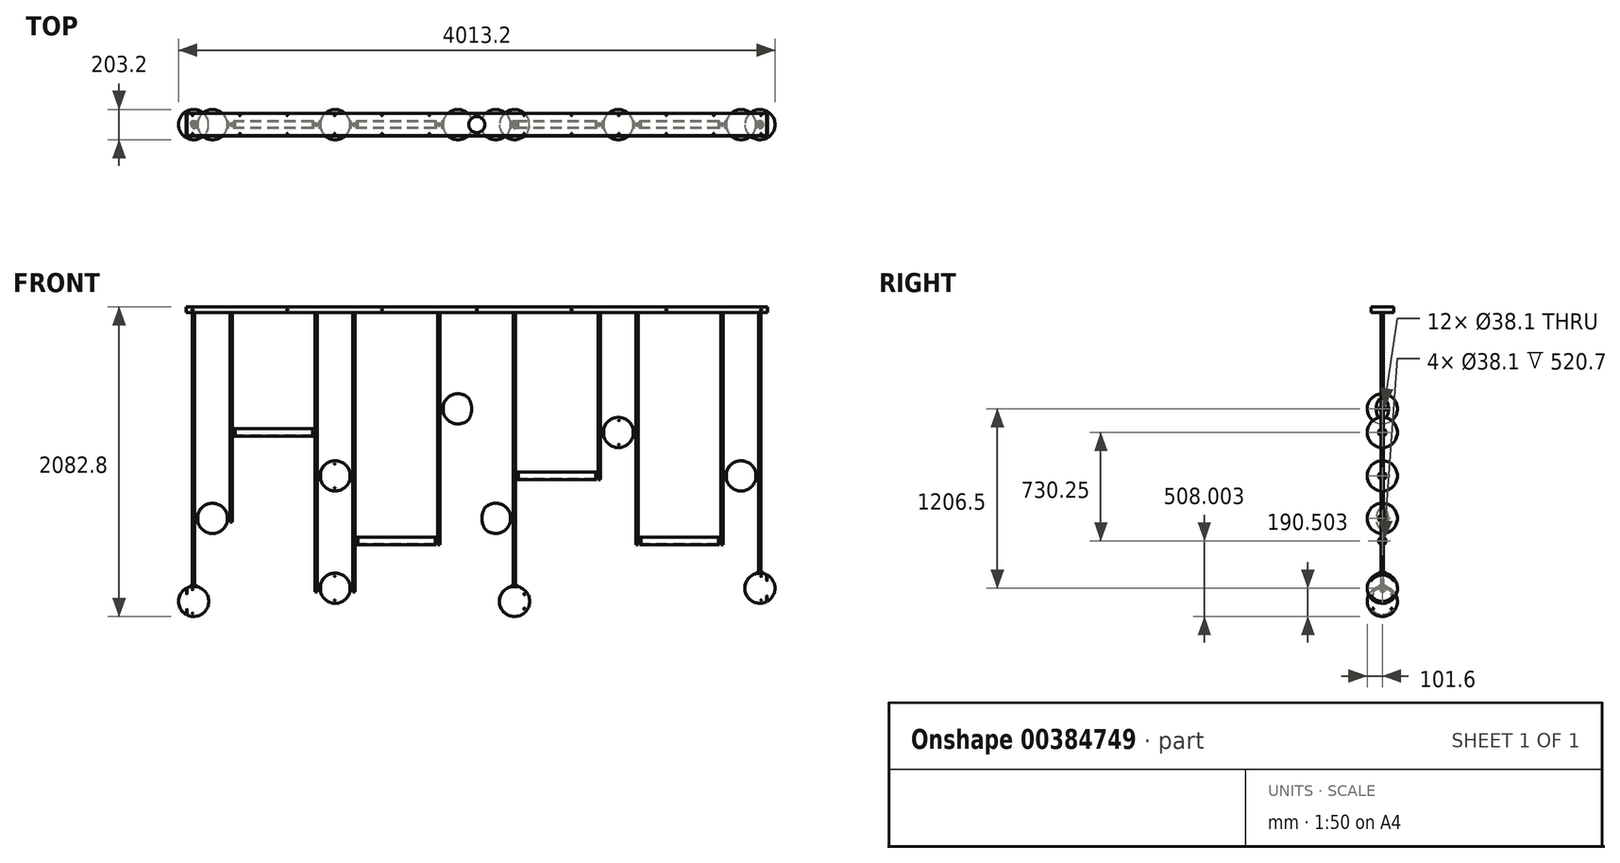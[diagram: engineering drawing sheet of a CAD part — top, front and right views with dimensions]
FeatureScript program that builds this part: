
annotation { "Feature Type Name" : "Feature", "Feature Type Description" : "" }
export const myFeature = defineFeature(function(context is Context, id is Id, definition is map)
    precondition{}
    {
        {
            var Q0;
            Q0=qCreatedBy(makeId("Front.planeOp"),FACE);
            var sketch = newSketch(context, id + "F0", { "sketchPlane" : qUnion([Q0])});
            skLineSegment(sketch, "E0.bottom", {"start": v(-1955.8, 1091.47) * mm, "end": v(1955.8, 1091.47) * mm});
            skLineSegment(sketch, "E0.top", {"start": v(-1955.8, 1053.37) * mm, "end": v(1955.8, 1053.37) * mm});
            skLineSegment(sketch, "E0.left", {"start": v(-1955.8, 1091.47) * mm, "end": v(-1955.8, 1053.37) * mm});
            skLineSegment(sketch, "E0.right", {"start": v(1955.8, 1091.47) * mm, "end": v(1955.8, 1053.37) * mm});
            skLineSegment(sketch, "E1", {"start": v(0, 0) * mm, "end": v(0, 1053.37) * mm, "construction": true});
            skLineSegment(sketch, "E2", {"start": v(-1905, 1053.37) * mm, "end": v(-1905, -788.13) * mm, "construction": true});
            skCircle(sketch, "E3", {"center": v(-1905, -889.73) * mm, "radius": 101.6 * mm});
            skLineSegment(sketch, "E4", {"start": v(-1651, 1053.37) * mm, "end": v(-1651, -788.13) * mm, "construction": true});
            skLineSegment(sketch, "E5", {"start": v(-1079.5, 1053.37) * mm, "end": v(-1079.5, -788.13) * mm, "construction": true});
            skLineSegment(sketch, "E6", {"start": v(-825.5, 1053.37) * mm, "end": v(-825.5, -788.13) * mm, "construction": true});
            skLineSegment(sketch, "E7", {"start": v(-254, 1053.37) * mm, "end": v(-254, -788.13) * mm, "construction": true});
            skLineSegment(sketch, "E8", {"start": v(0, 1053.37) * mm, "end": v(0, -788.13) * mm, "construction": true});
            skLineSegment(sketch, "E9", {"start": v(254, 1053.37) * mm, "end": v(254, -788.13) * mm, "construction": true});
            skLineSegment(sketch, "E10", {"start": v(-1905, -788.13) * mm, "end": v(1787.4, -788.13) * mm, "construction": true});
            skLineSegment(sketch, "E11", {"start": v(825.5, 1053.37) * mm, "end": v(825.5, -788.13) * mm, "construction": true});
            skLineSegment(sketch, "E12", {"start": v(1079.5, 1053.37) * mm, "end": v(1079.5, -788.13) * mm, "construction": true});
            skLineSegment(sketch, "E13", {"start": v(1651, 1053.37) * mm, "end": v(1651, -788.13) * mm, "construction": true});
            skLineSegment(sketch, "E14", {"start": v(1905, 1053.37) * mm, "end": v(1905, -788.13) * mm, "construction": true});
            skLineSegment(sketch, "E15", {"start": v(-1955.8, 1091.47) * mm, "end": v(-1955.8, -788.13) * mm, "construction": true});
            skLineSegment(sketch, "E16", {"start": v(1955.8, 1053.37) * mm, "end": v(1955.8, -788.13) * mm, "construction": true});
            skLineSegment(sketch, "E17", {"start": v(1955.8, -91.24) * mm, "end": v(1905, -91.24) * mm, "construction": true});
            skLineSegment(sketch, "E18", {"start": v(-1955.8, -396.8) * mm, "end": v(-1905, -396.8) * mm, "construction": true});
            skLineSegment(sketch, "E19", {"start": v(-1651, 246.92) * mm, "end": v(-1079.5, 246.92) * mm, "construction": true});
            skLineSegment(sketch, "E20", {"start": v(1079.5, -483.33) * mm, "end": v(1651, -483.33) * mm, "construction": true});
            skLineSegment(sketch, "E21", {"start": v(-1079.5, -45.18) * mm, "end": v(-825.5, -45.18) * mm, "construction": true});
            skLineSegment(sketch, "E22", {"start": v(-254, 405.67) * mm, "end": v(0, 405.67) * mm, "construction": true});
            skLineSegment(sketch, "E23", {"start": v(0, -330.93) * mm, "end": v(254, -330.93) * mm, "construction": true});
            skLineSegment(sketch, "E24", {"start": v(1651, -45.18) * mm, "end": v(1905, -45.18) * mm, "construction": true});
            skLineSegment(sketch, "E25", {"start": v(-1905, -330.93) * mm, "end": v(-1651, -330.93) * mm, "construction": true});
            skCircle(sketch, "E26", {"center": v(-1778, -330.93) * mm, "radius": 101.6 * mm});
            skCircle(sketch, "E27", {"center": v(-952.5, -45.18) * mm, "radius": 101.6 * mm});
            skCircle(sketch, "E28", {"center": v(-127, 405.67) * mm, "radius": 101.6 * mm});
            skCircle(sketch, "E29", {"center": v(127, -330.93) * mm, "radius": 101.6 * mm});
            skCircle(sketch, "E30", {"center": v(1778, -45.18) * mm, "radius": 101.6 * mm});
            skLineSegment(sketch, "E31", {"start": v(-1079.5, -800.83) * mm, "end": v(-825.5, -800.83) * mm, "construction": true});
            skCircle(sketch, "E32", {"center": v(-952.5, -800.83) * mm, "radius": 101.6 * mm});
            skCircle(sketch, "E33", {"center": v(254, -889.73) * mm, "radius": 101.6 * mm});
            skCircle(sketch, "E34", {"center": v(1905, -800.83) * mm, "radius": 101.6 * mm});
            skLineSegment(sketch, "E35", {"start": v(254, -991.33) * mm, "end": v(-1905, -991.33) * mm, "construction": true});
            skLineSegment(sketch, "E36.bottom", {"start": v(-1625.6, 272.32) * mm, "end": v(-1104.9, 272.32) * mm});
            skLineSegment(sketch, "E36.top", {"start": v(-1625.6, 221.52) * mm, "end": v(-1104.9, 221.52) * mm});
            skLineSegment(sketch, "E36.left", {"start": v(-1625.6, 272.32) * mm, "end": v(-1625.6, 221.52) * mm});
            skLineSegment(sketch, "E36.right", {"start": v(-1104.9, 272.32) * mm, "end": v(-1104.9, 221.52) * mm});
            skPoint(sketch, "E36.middle", {"position": v(-1365.25, 246.92) * mm});
            skLineSegment(sketch, "E37.bottom", {"start": v(1104.9, -457.93) * mm, "end": v(1625.6, -457.93) * mm});
            skLineSegment(sketch, "E37.top", {"start": v(1104.9, -508.73) * mm, "end": v(1625.6, -508.73) * mm});
            skLineSegment(sketch, "E37.left", {"start": v(1104.9, -457.93) * mm, "end": v(1104.9, -508.73) * mm});
            skLineSegment(sketch, "E37.right", {"start": v(1625.6, -457.93) * mm, "end": v(1625.6, -508.73) * mm});
            skPoint(sketch, "E37.middle", {"position": v(1365.25, -483.33) * mm});
            skLineSegment(sketch, "E38", {"start": v(254, -45.18) * mm, "end": v(825.5, -45.18) * mm, "construction": true});
            skLineSegment(sketch, "E39.bottom", {"start": v(800.1, -70.58) * mm, "end": v(279.4, -70.58) * mm});
            skLineSegment(sketch, "E39.top", {"start": v(800.1, -19.78) * mm, "end": v(279.4, -19.78) * mm});
            skLineSegment(sketch, "E39.left", {"start": v(800.1, -19.78) * mm, "end": v(800.1, -70.58) * mm});
            skLineSegment(sketch, "E39.right", {"start": v(279.4, -19.78) * mm, "end": v(279.4, -70.58) * mm});
            skPoint(sketch, "E39.middle", {"position": v(539.75, -45.18) * mm});
            skLineSegment(sketch, "E40", {"start": v(825.5, 246.92) * mm, "end": v(1079.5, 246.92) * mm, "construction": true});
            skCircle(sketch, "E41", {"center": v(952.5, 246.92) * mm, "radius": 101.6 * mm});
            skLineSegment(sketch, "E42", {"start": v(-825.5, -483.33) * mm, "end": v(-254, -483.33) * mm, "construction": true});
            skLineSegment(sketch, "E43.bottom", {"start": v(-800.1, -457.93) * mm, "end": v(-279.4, -457.93) * mm});
            skLineSegment(sketch, "E43.top", {"start": v(-800.1, -508.73) * mm, "end": v(-279.4, -508.73) * mm});
            skLineSegment(sketch, "E43.left", {"start": v(-800.1, -457.93) * mm, "end": v(-800.1, -508.73) * mm});
            skLineSegment(sketch, "E43.right", {"start": v(-279.4, -457.93) * mm, "end": v(-279.4, -508.73) * mm});
            skPoint(sketch, "E43.middle", {"position": v(-539.75, -483.33) * mm});
            skLineSegment(sketch, "E44", {"start": v(127, -330.93) * mm, "end": v(127, 405.67) * mm, "construction": true});
            skLineSegment(sketch, "E45", {"start": v(-952.5, -45.18) * mm, "end": v(-952.5, -800.83) * mm, "construction": true});
            skLineSegment(sketch, "E46", {"start": v(-127, 405.67) * mm, "end": v(-127, -800.83) * mm, "construction": true});
            skLineSegment(sketch, "E47", {"start": v(952.5, 246.92) * mm, "end": v(952.5, -330.93) * mm, "construction": true});
            skLineSegment(sketch, "E48", {"start": v(1778, -45.18) * mm, "end": v(1778, 246.92) * mm, "construction": true});
            skLineSegment(sketch, "E49", {"start": v(-1206.5, -45.18) * mm, "end": v(-1206.5, -330.93) * mm, "construction": true});
            skLineSegment(sketch, "E50", {"start": v(-1778, 0) * mm, "end": v(-952.5, 0) * mm, "construction": true});
            skLineSegment(sketch, "E51", {"start": v(-952.5, -423) * mm, "end": v(-127, -423) * mm, "construction": true});
            skLineSegment(sketch, "E52", {"start": v(127, 0) * mm, "end": v(952.5, 0) * mm, "construction": true});
            skLineSegment(sketch, "E53", {"start": v(952.5, 686.49) * mm, "end": v(1778, 686.49) * mm, "construction": true});
            skLineSegment(sketch, "E54", {"start": v(254, -991.33) * mm, "end": v(1905, -991.33) * mm, "construction": true});
            skLineSegment(sketch, "E55", {"start": v(1905, -800.83) * mm, "end": v(1905, -889.73) * mm, "construction": true});
            skSolve(sketch);
        }
        {
            var Q0;
            Q0=qCreatedBy(makeId("Front.planeOp"),FACE);
            var sketch = newSketch(context, id + "F1", { "sketchPlane" : qUnion([Q0])});
            skLineSegment(sketch, "E56.0.0", {"start": v(-1955.8, 1091.47) * mm, "end": v(-1955.8, 1053.37) * mm});
            skLineSegment(sketch, "E56.0.1", {"start": v(-1955.8, 1053.37) * mm, "end": v(1955.8, 1053.37) * mm});
            skLineSegment(sketch, "E56.0.2", {"start": v(1955.8, 1053.37) * mm, "end": v(1955.8, 1091.47) * mm});
            skLineSegment(sketch, "E56.0.3", {"start": v(1955.8, 1091.47) * mm, "end": v(-1955.8, 1091.47) * mm});
            skSolve(sketch);
        }
        {
            var Q0;
            Q0 = qSketchRegion(id + "F1", true);
            extrude(context, id + "F2", {"entities" : qUnion([Q0]), "depth" : 76.2 * mm, "hasSecondDirection" : true, "secondDirectionOppositeDirection" : true, "secondDirectionDepth" : 76.2 * mm});
        }
        {
            var Q0;
            Q0=qCreatedBy(makeId("Front.planeOp"),FACE);
            var sketch = newSketch(context, id + "F3", { "sketchPlane" : qUnion([Q0])});
            skArc(sketch, "E57.6", {"start": v(-1678.2, -311.88) * mm, "mid": v(-1778, -229.33) * mm, "end": v(-1877.8, -311.88) * mm});
            skArc(sketch, "E58.0", {"start": v(-1679.82, -311.88) * mm, "mid": v(-1778, -230.91) * mm, "end": v(-1876.18, -311.88) * mm});
            skLineSegment(sketch, "E59.0", {"start": v(-1905, -349.98) * mm, "end": v(-1651, -349.98) * mm, "construction": true});
            skLineSegment(sketch, "E60.0", {"start": v(-1905, -330.93) * mm, "end": v(-1651, -330.93) * mm, "construction": true});
            skLineSegment(sketch, "E61.MirrorCS", {"start": v(-1905, -311.88) * mm, "end": v(-1651, -311.88) * mm, "construction": true});
            skLineSegment(sketch, "E62", {"start": v(-1679.82, -311.88) * mm, "end": v(-1678.2, -311.88) * mm});
            skLineSegment(sketch, "E63", {"start": v(-1877.8, -311.88) * mm, "end": v(-1876.18, -311.88) * mm});
            skSolve(sketch);
        }
        {
            var Q0;
            Q0 = qSketchRegion(id + "F3", true);
            var Q1;
            Q1=sQuery(id+"F3.wireOp",EDGE,"E60.0");
            revolve(context, id + "F4", {"entities" : qUnion([Q0]), "axis" : qUnion([Q1]), "revolveType" : RevolveType.FULL});
        }
        {
            var Q0;
            Q0=qCreatedBy(makeId("Front.planeOp"),FACE);
            var sketch = newSketch(context, id + "F5", { "sketchPlane" : qUnion([Q0])});
            skLineSegment(sketch, "E64.0", {"start": v(-1678.2, -349.98) * mm, "end": v(-1678.2, -311.88) * mm, "construction": true});
            skCircle(sketch, "E65.1", {"center": v(-1778, -330.93) * mm, "radius": 101.6 * mm, "construction": true});
            skLineSegment(sketch, "E66.bottom", {"start": v(-1671.69, -330.93) * mm, "end": v(-1679.63, -330.93) * mm});
            skLineSegment(sketch, "E66.top", {"start": v(-1671.69, -305.53) * mm, "end": v(-1679.63, -305.53) * mm});
            skLineSegment(sketch, "E66.left", {"start": v(-1671.69, -330.93) * mm, "end": v(-1671.69, -305.53) * mm});
            skLineSegment(sketch, "E66.right", {"start": v(-1679.63, -330.93) * mm, "end": v(-1679.63, -305.53) * mm});
            skLineSegment(sketch, "E67.bottom", {"start": v(-1671.69, -330.93) * mm, "end": v(-1651, -330.93) * mm});
            skLineSegment(sketch, "E67.top", {"start": v(-1671.69, -324.58) * mm, "end": v(-1651, -324.58) * mm});
            skLineSegment(sketch, "E67.left", {"start": v(-1671.69, -330.93) * mm, "end": v(-1671.69, -324.58) * mm});
            skLineSegment(sketch, "E67.right", {"start": v(-1651, -330.93) * mm, "end": v(-1651, -324.58) * mm});
            skLineSegment(sketch, "E68.0", {"start": v(-1651, 1053.37) * mm, "end": v(-1651, -788.13) * mm, "construction": true});
            skLineSegment(sketch, "E69", {"start": v(-1778, -330.93) * mm, "end": v(-1778, -333.62) * mm, "construction": true});
            skLineSegment(sketch, "E70.MirrorCS", {"start": v(-1884.31, -305.53) * mm, "end": v(-1876.37, -305.53) * mm});
            skLineSegment(sketch, "E71.MirrorCS", {"start": v(-1884.31, -330.93) * mm, "end": v(-1876.37, -330.93) * mm});
            skLineSegment(sketch, "E72.MirrorCS", {"start": v(-1905, -330.93) * mm, "end": v(-1905, -324.58) * mm});
            skLineSegment(sketch, "E73.MirrorCS", {"start": v(-1884.31, -330.93) * mm, "end": v(-1884.31, -324.58) * mm});
            skLineSegment(sketch, "E74.MirrorCS", {"start": v(-1884.31, -324.58) * mm, "end": v(-1905, -324.58) * mm});
            skLineSegment(sketch, "E75.MirrorCS", {"start": v(-1884.31, -330.93) * mm, "end": v(-1905, -330.93) * mm});
            skLineSegment(sketch, "E76.MirrorCS", {"start": v(-1876.37, -330.93) * mm, "end": v(-1876.37, -305.53) * mm});
            skLineSegment(sketch, "E77.MirrorCS", {"start": v(-1884.31, -330.93) * mm, "end": v(-1884.31, -305.53) * mm});
            skSolve(sketch);
        }
        {
            var Q0;
            Q0 = qSketchRegion(id + "F5", true);
            var Q1;
            Q1=sQuery(id+"F5.wireOp",EDGE,"E67.bottom");
            revolve(context, id + "F6", {"entities" : qUnion([Q0]), "axis" : qUnion([Q1]), "revolveType" : RevolveType.FULL});
        }
        {
            var Q0;
            Q0=qCreatedBy(makeId("Front.planeOp"),FACE);
            var sketch = newSketch(context, id + "F7", { "sketchPlane" : qUnion([Q0])});
            skLineSegment(sketch, "E78.0", {"start": v(-1905, 1053.37) * mm, "end": v(-1905, -788.13) * mm, "construction": true});
            skLineSegment(sketch, "E79.0", {"start": v(-1905, -330.93) * mm, "end": v(-1651, -330.93) * mm, "construction": true});
            skLineSegment(sketch, "E80", {"start": v(-1778, -330.93) * mm, "end": v(-1778, -44.72) * mm, "construction": true});
            skLineSegment(sketch, "E81.bottom", {"start": v(-1905, -305.53) * mm, "end": v(-1912.94, -305.53) * mm});
            skLineSegment(sketch, "E81.top", {"start": v(-1905, -356.33) * mm, "end": v(-1912.94, -356.33) * mm});
            skLineSegment(sketch, "E81.left", {"start": v(-1905, -305.53) * mm, "end": v(-1905, -356.33) * mm});
            skLineSegment(sketch, "E81.right", {"start": v(-1912.94, -305.53) * mm, "end": v(-1912.94, -356.33) * mm});
            skPoint(sketch, "E82", {"position": v(-1905, -330.93) * mm});
            skLineSegment(sketch, "E83.MirrorCS", {"start": v(-1643.06, -305.53) * mm, "end": v(-1643.06, -356.33) * mm});
            skLineSegment(sketch, "E84.MirrorCS", {"start": v(-1651, -305.53) * mm, "end": v(-1651, -356.33) * mm});
            skLineSegment(sketch, "E85.MirrorCS", {"start": v(-1651, -356.33) * mm, "end": v(-1643.06, -356.33) * mm});
            skLineSegment(sketch, "E86.MirrorCS", {"start": v(-1651, -305.53) * mm, "end": v(-1643.06, -305.53) * mm});
            skPoint(sketch, "E87.MirrorP", {"position": v(-1651, -330.93) * mm});
            skSolve(sketch);
        }
        {
            var Q0;
            Q0=makeQuery(id+"F7.imprint","IMPRINT",FACE,{"disambiguationData":[TD([[makeQuery(id+"F7.imprint","IMPRINT",EDGE,{"derivedFrom":sQuery(id+"F7.wireOp",EDGE,"E81.bottom")}),1.0]])]});
            var Q1;
            Q1=sQuery(id+"F7.wireOp",EDGE,"E78.0");
            revolve(context, id + "F8", {"entities" : qUnion([Q0]), "axis" : qUnion([Q1]), "revolveType" : RevolveType.FULL});
        }
        {
            var Q0;
            Q0=makeQuery(id+"F7.imprint","IMPRINT",FACE,{"disambiguationData":[TD([[makeQuery(id+"F7.imprint","IMPRINT",EDGE,{"derivedFrom":sQuery(id+"F7.wireOp",EDGE,"E83.MirrorCS")}),-1.0]])]});
            var Q1;
            Q1=sQuery(id+"F0.wireOp",EDGE,"E4");
            revolve(context, id + "F9", {"entities" : qUnion([Q0]), "axis" : qUnion([Q1]), "revolveType" : RevolveType.FULL});
        }
        {
            var Q0;
            Q0=makeQuery(id+"F6.opRevolve","SWEPT_BODY",BODY,{"disambiguationData":[OSD([sQuery(id+"F5.wireOp",EDGE,"E70.MirrorCS"),sQuery(id+"F5.wireOp",EDGE,"E71.MirrorCS"),sQuery(id+"F5.wireOp",EDGE,"E72.MirrorCS"),sQuery(id+"F5.wireOp",EDGE,"E74.MirrorCS"),sQuery(id+"F5.wireOp",EDGE,"E75.MirrorCS"),sQuery(id+"F5.wireOp",EDGE,"E76.MirrorCS"),sQuery(id+"F5.wireOp",EDGE,"E77.MirrorCS")])]});
            var Q1;
            Q1=makeQuery(id+"F6.opRevolve","SWEPT_BODY",BODY,{"disambiguationData":[OSD([sQuery(id+"F5.wireOp",EDGE,"E66.bottom"),sQuery(id+"F5.wireOp",EDGE,"E66.top"),sQuery(id+"F5.wireOp",EDGE,"E66.left"),sQuery(id+"F5.wireOp",EDGE,"E66.right"),sQuery(id+"F5.wireOp",EDGE,"E67.bottom"),sQuery(id+"F5.wireOp",EDGE,"E67.top"),sQuery(id+"F5.wireOp",EDGE,"E67.right")])]});
            var Q2;
            Q2=makeQuery(id+"F4.opRevolve","SWEPT_BODY",BODY,{"disambiguationData":[OSD([sQuery(id+"F3.wireOp",EDGE,"E57.6"),sQuery(id+"F3.wireOp",EDGE,"E58.0"),sQuery(id+"F3.wireOp",EDGE,"E62"),sQuery(id+"F3.wireOp",EDGE,"E63")])]});
            var Q3;
            Q3=makeQuery(id+"F8.opRevolve","SWEPT_BODY",BODY,{"disambiguationData":[OSD([sQuery(id+"F7.wireOp",EDGE,"E81.bottom"),sQuery(id+"F7.wireOp",EDGE,"E81.top"),sQuery(id+"F7.wireOp",EDGE,"E81.left"),sQuery(id+"F7.wireOp",EDGE,"E81.right")])]});
            var Q4;
            Q4=makeQuery(id+"F9.opRevolve","SWEPT_BODY",BODY,{"disambiguationData":[OSD([sQuery(id+"F7.wireOp",EDGE,"E83.MirrorCS"),sQuery(id+"F7.wireOp",EDGE,"E84.MirrorCS"),sQuery(id+"F7.wireOp",EDGE,"E85.MirrorCS"),sQuery(id+"F7.wireOp",EDGE,"E86.MirrorCS")])]});
            var Q5;
            Q5=sQuery(id+"F0.wireOp",EDGE,"E50");
            transform(context, id + "F10", {"entities" : qUnion([Q0, Q1, Q2, Q3, Q4]), "transformType" : TransformType.TRANSLATION_ENTITY, "oppositeDirectionEntity" : false, "transformLine" : qUnion([Q5]), "makeCopy" : true});
        }
        {
            var Q0;
            Q0=makeQuery(id+"F10.opPattern","COPY",BODY,{"derivedFrom":makeQuery(id+"F6.opRevolve","SWEPT_BODY",BODY,{"disambiguationData":[OSD([sQuery(id+"F5.wireOp",EDGE,"E66.bottom"),sQuery(id+"F5.wireOp",EDGE,"E66.top"),sQuery(id+"F5.wireOp",EDGE,"E66.left"),sQuery(id+"F5.wireOp",EDGE,"E66.right"),sQuery(id+"F5.wireOp",EDGE,"E67.bottom"),sQuery(id+"F5.wireOp",EDGE,"E67.top"),sQuery(id+"F5.wireOp",EDGE,"E67.right")])]}),"instanceName":"1"});
            var Q1;
            Q1=makeQuery(id+"F10.opPattern","COPY",BODY,{"derivedFrom":makeQuery(id+"F4.opRevolve","SWEPT_BODY",BODY,{"disambiguationData":[OSD([sQuery(id+"F3.wireOp",EDGE,"E57.6"),sQuery(id+"F3.wireOp",EDGE,"E58.0"),sQuery(id+"F3.wireOp",EDGE,"E62"),sQuery(id+"F3.wireOp",EDGE,"E63")])]}),"instanceName":"1"});
            var Q2;
            Q2=makeQuery(id+"F10.opPattern","COPY",BODY,{"derivedFrom":makeQuery(id+"F6.opRevolve","SWEPT_BODY",BODY,{"disambiguationData":[OSD([sQuery(id+"F5.wireOp",EDGE,"E70.MirrorCS"),sQuery(id+"F5.wireOp",EDGE,"E71.MirrorCS"),sQuery(id+"F5.wireOp",EDGE,"E72.MirrorCS"),sQuery(id+"F5.wireOp",EDGE,"E74.MirrorCS"),sQuery(id+"F5.wireOp",EDGE,"E75.MirrorCS"),sQuery(id+"F5.wireOp",EDGE,"E76.MirrorCS"),sQuery(id+"F5.wireOp",EDGE,"E77.MirrorCS")])]}),"instanceName":"1"});
            var Q3;
            Q3=makeQuery(id+"F10.opPattern","COPY",BODY,{"derivedFrom":makeQuery(id+"F8.opRevolve","SWEPT_BODY",BODY,{"disambiguationData":[OSD([sQuery(id+"F7.wireOp",EDGE,"E81.bottom"),sQuery(id+"F7.wireOp",EDGE,"E81.top"),sQuery(id+"F7.wireOp",EDGE,"E81.left"),sQuery(id+"F7.wireOp",EDGE,"E81.right")])]}),"instanceName":"1"});
            var Q4;
            Q4=makeQuery(id+"F10.opPattern","COPY",BODY,{"derivedFrom":makeQuery(id+"F9.opRevolve","SWEPT_BODY",BODY,{"disambiguationData":[OSD([sQuery(id+"F7.wireOp",EDGE,"E83.MirrorCS"),sQuery(id+"F7.wireOp",EDGE,"E84.MirrorCS"),sQuery(id+"F7.wireOp",EDGE,"E85.MirrorCS"),sQuery(id+"F7.wireOp",EDGE,"E86.MirrorCS")])]}),"instanceName":"1"});
            var Q5;
            Q5=sQuery(id+"F0.wireOp",EDGE,"E49");
            transform(context, id + "F11", {"entities" : qUnion([Q0, Q1, Q2, Q3, Q4]), "transformType" : TransformType.TRANSLATION_ENTITY, "oppositeDirectionEntity" : true, "transformLine" : qUnion([Q5]), "makeCopy" : false});
        }
        {
            var Q0;
            Q0=makeQuery(id+"F10.opPattern","COPY",BODY,{"derivedFrom":makeQuery(id+"F4.opRevolve","SWEPT_BODY",BODY,{"disambiguationData":[OSD([sQuery(id+"F3.wireOp",EDGE,"E57.6"),sQuery(id+"F3.wireOp",EDGE,"E58.0"),sQuery(id+"F3.wireOp",EDGE,"E62"),sQuery(id+"F3.wireOp",EDGE,"E63")])]}),"instanceName":"1"});
            var Q1;
            Q1=makeQuery(id+"F10.opPattern","COPY",BODY,{"derivedFrom":makeQuery(id+"F6.opRevolve","SWEPT_BODY",BODY,{"disambiguationData":[OSD([sQuery(id+"F5.wireOp",EDGE,"E66.bottom"),sQuery(id+"F5.wireOp",EDGE,"E66.top"),sQuery(id+"F5.wireOp",EDGE,"E66.left"),sQuery(id+"F5.wireOp",EDGE,"E66.right"),sQuery(id+"F5.wireOp",EDGE,"E67.bottom"),sQuery(id+"F5.wireOp",EDGE,"E67.top"),sQuery(id+"F5.wireOp",EDGE,"E67.right")])]}),"instanceName":"1"});
            var Q2;
            Q2=makeQuery(id+"F10.opPattern","COPY",BODY,{"derivedFrom":makeQuery(id+"F6.opRevolve","SWEPT_BODY",BODY,{"disambiguationData":[OSD([sQuery(id+"F5.wireOp",EDGE,"E70.MirrorCS"),sQuery(id+"F5.wireOp",EDGE,"E71.MirrorCS"),sQuery(id+"F5.wireOp",EDGE,"E72.MirrorCS"),sQuery(id+"F5.wireOp",EDGE,"E74.MirrorCS"),sQuery(id+"F5.wireOp",EDGE,"E75.MirrorCS"),sQuery(id+"F5.wireOp",EDGE,"E76.MirrorCS"),sQuery(id+"F5.wireOp",EDGE,"E77.MirrorCS")])]}),"instanceName":"1"});
            var Q3;
            Q3=makeQuery(id+"F10.opPattern","COPY",BODY,{"derivedFrom":makeQuery(id+"F8.opRevolve","SWEPT_BODY",BODY,{"disambiguationData":[OSD([sQuery(id+"F7.wireOp",EDGE,"E81.bottom"),sQuery(id+"F7.wireOp",EDGE,"E81.top"),sQuery(id+"F7.wireOp",EDGE,"E81.left"),sQuery(id+"F7.wireOp",EDGE,"E81.right")])]}),"instanceName":"1"});
            var Q4;
            Q4=makeQuery(id+"F10.opPattern","COPY",BODY,{"derivedFrom":makeQuery(id+"F9.opRevolve","SWEPT_BODY",BODY,{"disambiguationData":[OSD([sQuery(id+"F7.wireOp",EDGE,"E83.MirrorCS"),sQuery(id+"F7.wireOp",EDGE,"E84.MirrorCS"),sQuery(id+"F7.wireOp",EDGE,"E85.MirrorCS"),sQuery(id+"F7.wireOp",EDGE,"E86.MirrorCS")])]}),"instanceName":"1"});
            var Q5;
            Q5=sQuery(id+"F0.wireOp",EDGE,"E45");
            transform(context, id + "F12", {"entities" : qUnion([Q0, Q1, Q2, Q3, Q4]), "transformType" : TransformType.TRANSLATION_ENTITY, "oppositeDirectionEntity" : false, "transformLine" : qUnion([Q5]), "makeCopy" : true});
        }
        {
            var Q0;
            Q0=makeQuery(id+"F12.opPattern","COPY",BODY,{"derivedFrom":makeQuery(id+"F10.opPattern","COPY",BODY,{"derivedFrom":makeQuery(id+"F4.opRevolve","SWEPT_BODY",BODY,{"disambiguationData":[OSD([sQuery(id+"F3.wireOp",EDGE,"E57.6"),sQuery(id+"F3.wireOp",EDGE,"E58.0"),sQuery(id+"F3.wireOp",EDGE,"E62"),sQuery(id+"F3.wireOp",EDGE,"E63")])]}),"instanceName":"1"}),"instanceName":"1"});
            var Q1;
            Q1=makeQuery(id+"F12.opPattern","COPY",BODY,{"derivedFrom":makeQuery(id+"F10.opPattern","COPY",BODY,{"derivedFrom":makeQuery(id+"F6.opRevolve","SWEPT_BODY",BODY,{"disambiguationData":[OSD([sQuery(id+"F5.wireOp",EDGE,"E66.bottom"),sQuery(id+"F5.wireOp",EDGE,"E66.top"),sQuery(id+"F5.wireOp",EDGE,"E66.left"),sQuery(id+"F5.wireOp",EDGE,"E66.right"),sQuery(id+"F5.wireOp",EDGE,"E67.bottom"),sQuery(id+"F5.wireOp",EDGE,"E67.top"),sQuery(id+"F5.wireOp",EDGE,"E67.right")])]}),"instanceName":"1"}),"instanceName":"1"});
            var Q2;
            Q2=makeQuery(id+"F12.opPattern","COPY",BODY,{"derivedFrom":makeQuery(id+"F10.opPattern","COPY",BODY,{"derivedFrom":makeQuery(id+"F6.opRevolve","SWEPT_BODY",BODY,{"disambiguationData":[OSD([sQuery(id+"F5.wireOp",EDGE,"E70.MirrorCS"),sQuery(id+"F5.wireOp",EDGE,"E71.MirrorCS"),sQuery(id+"F5.wireOp",EDGE,"E72.MirrorCS"),sQuery(id+"F5.wireOp",EDGE,"E74.MirrorCS"),sQuery(id+"F5.wireOp",EDGE,"E75.MirrorCS"),sQuery(id+"F5.wireOp",EDGE,"E76.MirrorCS"),sQuery(id+"F5.wireOp",EDGE,"E77.MirrorCS")])]}),"instanceName":"1"}),"instanceName":"1"});
            var Q3;
            Q3=makeQuery(id+"F12.opPattern","COPY",BODY,{"derivedFrom":makeQuery(id+"F10.opPattern","COPY",BODY,{"derivedFrom":makeQuery(id+"F8.opRevolve","SWEPT_BODY",BODY,{"disambiguationData":[OSD([sQuery(id+"F7.wireOp",EDGE,"E81.bottom"),sQuery(id+"F7.wireOp",EDGE,"E81.top"),sQuery(id+"F7.wireOp",EDGE,"E81.left"),sQuery(id+"F7.wireOp",EDGE,"E81.right")])]}),"instanceName":"1"}),"instanceName":"1"});
            var Q4;
            Q4=makeQuery(id+"F12.opPattern","COPY",BODY,{"derivedFrom":makeQuery(id+"F10.opPattern","COPY",BODY,{"derivedFrom":makeQuery(id+"F9.opRevolve","SWEPT_BODY",BODY,{"disambiguationData":[OSD([sQuery(id+"F7.wireOp",EDGE,"E83.MirrorCS"),sQuery(id+"F7.wireOp",EDGE,"E84.MirrorCS"),sQuery(id+"F7.wireOp",EDGE,"E85.MirrorCS"),sQuery(id+"F7.wireOp",EDGE,"E86.MirrorCS")])]}),"instanceName":"1"}),"instanceName":"1"});
            var Q5;
            Q5=sQuery(id+"F0.wireOp",EDGE,"E51");
            transform(context, id + "F13", {"entities" : qUnion([Q0, Q1, Q2, Q3, Q4]), "transformType" : TransformType.TRANSLATION_ENTITY, "oppositeDirectionEntity" : false, "transformLine" : qUnion([Q5]), "makeCopy" : true});
        }
        {
            var Q0;
            Q0=makeQuery(id+"F13.opPattern","COPY",BODY,{"derivedFrom":makeQuery(id+"F12.opPattern","COPY",BODY,{"derivedFrom":makeQuery(id+"F10.opPattern","COPY",BODY,{"derivedFrom":makeQuery(id+"F6.opRevolve","SWEPT_BODY",BODY,{"disambiguationData":[OSD([sQuery(id+"F5.wireOp",EDGE,"E66.bottom"),sQuery(id+"F5.wireOp",EDGE,"E66.top"),sQuery(id+"F5.wireOp",EDGE,"E66.left"),sQuery(id+"F5.wireOp",EDGE,"E66.right"),sQuery(id+"F5.wireOp",EDGE,"E67.bottom"),sQuery(id+"F5.wireOp",EDGE,"E67.top"),sQuery(id+"F5.wireOp",EDGE,"E67.right")])]}),"instanceName":"1"}),"instanceName":"1"}),"instanceName":"1"});
            var Q1;
            Q1=makeQuery(id+"F13.opPattern","COPY",BODY,{"derivedFrom":makeQuery(id+"F12.opPattern","COPY",BODY,{"derivedFrom":makeQuery(id+"F10.opPattern","COPY",BODY,{"derivedFrom":makeQuery(id+"F4.opRevolve","SWEPT_BODY",BODY,{"disambiguationData":[OSD([sQuery(id+"F3.wireOp",EDGE,"E57.6"),sQuery(id+"F3.wireOp",EDGE,"E58.0"),sQuery(id+"F3.wireOp",EDGE,"E62"),sQuery(id+"F3.wireOp",EDGE,"E63")])]}),"instanceName":"1"}),"instanceName":"1"}),"instanceName":"1"});
            var Q2;
            Q2=makeQuery(id+"F13.opPattern","COPY",BODY,{"derivedFrom":makeQuery(id+"F12.opPattern","COPY",BODY,{"derivedFrom":makeQuery(id+"F10.opPattern","COPY",BODY,{"derivedFrom":makeQuery(id+"F6.opRevolve","SWEPT_BODY",BODY,{"disambiguationData":[OSD([sQuery(id+"F5.wireOp",EDGE,"E70.MirrorCS"),sQuery(id+"F5.wireOp",EDGE,"E71.MirrorCS"),sQuery(id+"F5.wireOp",EDGE,"E72.MirrorCS"),sQuery(id+"F5.wireOp",EDGE,"E74.MirrorCS"),sQuery(id+"F5.wireOp",EDGE,"E75.MirrorCS"),sQuery(id+"F5.wireOp",EDGE,"E76.MirrorCS"),sQuery(id+"F5.wireOp",EDGE,"E77.MirrorCS")])]}),"instanceName":"1"}),"instanceName":"1"}),"instanceName":"1"});
            var Q3;
            Q3=makeQuery(id+"F13.opPattern","COPY",BODY,{"derivedFrom":makeQuery(id+"F12.opPattern","COPY",BODY,{"derivedFrom":makeQuery(id+"F10.opPattern","COPY",BODY,{"derivedFrom":makeQuery(id+"F8.opRevolve","SWEPT_BODY",BODY,{"disambiguationData":[OSD([sQuery(id+"F7.wireOp",EDGE,"E81.bottom"),sQuery(id+"F7.wireOp",EDGE,"E81.top"),sQuery(id+"F7.wireOp",EDGE,"E81.left"),sQuery(id+"F7.wireOp",EDGE,"E81.right")])]}),"instanceName":"1"}),"instanceName":"1"}),"instanceName":"1"});
            var Q4;
            Q4=makeQuery(id+"F13.opPattern","COPY",BODY,{"derivedFrom":makeQuery(id+"F12.opPattern","COPY",BODY,{"derivedFrom":makeQuery(id+"F10.opPattern","COPY",BODY,{"derivedFrom":makeQuery(id+"F9.opRevolve","SWEPT_BODY",BODY,{"disambiguationData":[OSD([sQuery(id+"F7.wireOp",EDGE,"E83.MirrorCS"),sQuery(id+"F7.wireOp",EDGE,"E84.MirrorCS"),sQuery(id+"F7.wireOp",EDGE,"E85.MirrorCS"),sQuery(id+"F7.wireOp",EDGE,"E86.MirrorCS")])]}),"instanceName":"1"}),"instanceName":"1"}),"instanceName":"1"});
            var Q5;
            Q5=sQuery(id+"F0.wireOp",EDGE,"E46");
            transform(context, id + "F14", {"entities" : qUnion([Q0, Q1, Q2, Q3, Q4]), "transformType" : TransformType.TRANSLATION_ENTITY, "oppositeDirectionEntity" : true, "transformLine" : qUnion([Q5]), "makeCopy" : true});
        }
        {
            var Q0;
            Q0=makeQuery(id+"F14.opPattern","COPY",BODY,{"derivedFrom":makeQuery(id+"F13.opPattern","COPY",BODY,{"derivedFrom":makeQuery(id+"F12.opPattern","COPY",BODY,{"derivedFrom":makeQuery(id+"F10.opPattern","COPY",BODY,{"derivedFrom":makeQuery(id+"F4.opRevolve","SWEPT_BODY",BODY,{"disambiguationData":[OSD([sQuery(id+"F3.wireOp",EDGE,"E57.6"),sQuery(id+"F3.wireOp",EDGE,"E58.0"),sQuery(id+"F3.wireOp",EDGE,"E62"),sQuery(id+"F3.wireOp",EDGE,"E63")])]}),"instanceName":"1"}),"instanceName":"1"}),"instanceName":"1"}),"instanceName":"1"});
            var Q1;
            Q1=makeQuery(id+"F14.opPattern","COPY",BODY,{"derivedFrom":makeQuery(id+"F13.opPattern","COPY",BODY,{"derivedFrom":makeQuery(id+"F12.opPattern","COPY",BODY,{"derivedFrom":makeQuery(id+"F10.opPattern","COPY",BODY,{"derivedFrom":makeQuery(id+"F6.opRevolve","SWEPT_BODY",BODY,{"disambiguationData":[OSD([sQuery(id+"F5.wireOp",EDGE,"E66.bottom"),sQuery(id+"F5.wireOp",EDGE,"E66.top"),sQuery(id+"F5.wireOp",EDGE,"E66.left"),sQuery(id+"F5.wireOp",EDGE,"E66.right"),sQuery(id+"F5.wireOp",EDGE,"E67.bottom"),sQuery(id+"F5.wireOp",EDGE,"E67.top"),sQuery(id+"F5.wireOp",EDGE,"E67.right")])]}),"instanceName":"1"}),"instanceName":"1"}),"instanceName":"1"}),"instanceName":"1"});
            var Q2;
            Q2=makeQuery(id+"F14.opPattern","COPY",BODY,{"derivedFrom":makeQuery(id+"F13.opPattern","COPY",BODY,{"derivedFrom":makeQuery(id+"F12.opPattern","COPY",BODY,{"derivedFrom":makeQuery(id+"F10.opPattern","COPY",BODY,{"derivedFrom":makeQuery(id+"F6.opRevolve","SWEPT_BODY",BODY,{"disambiguationData":[OSD([sQuery(id+"F5.wireOp",EDGE,"E70.MirrorCS"),sQuery(id+"F5.wireOp",EDGE,"E71.MirrorCS"),sQuery(id+"F5.wireOp",EDGE,"E72.MirrorCS"),sQuery(id+"F5.wireOp",EDGE,"E74.MirrorCS"),sQuery(id+"F5.wireOp",EDGE,"E75.MirrorCS"),sQuery(id+"F5.wireOp",EDGE,"E76.MirrorCS"),sQuery(id+"F5.wireOp",EDGE,"E77.MirrorCS")])]}),"instanceName":"1"}),"instanceName":"1"}),"instanceName":"1"}),"instanceName":"1"});
            var Q3;
            Q3=makeQuery(id+"F14.opPattern","COPY",BODY,{"derivedFrom":makeQuery(id+"F13.opPattern","COPY",BODY,{"derivedFrom":makeQuery(id+"F12.opPattern","COPY",BODY,{"derivedFrom":makeQuery(id+"F10.opPattern","COPY",BODY,{"derivedFrom":makeQuery(id+"F8.opRevolve","SWEPT_BODY",BODY,{"disambiguationData":[OSD([sQuery(id+"F7.wireOp",EDGE,"E81.bottom"),sQuery(id+"F7.wireOp",EDGE,"E81.top"),sQuery(id+"F7.wireOp",EDGE,"E81.left"),sQuery(id+"F7.wireOp",EDGE,"E81.right")])]}),"instanceName":"1"}),"instanceName":"1"}),"instanceName":"1"}),"instanceName":"1"});
            var Q4;
            Q4=makeQuery(id+"F14.opPattern","COPY",BODY,{"derivedFrom":makeQuery(id+"F13.opPattern","COPY",BODY,{"derivedFrom":makeQuery(id+"F12.opPattern","COPY",BODY,{"derivedFrom":makeQuery(id+"F10.opPattern","COPY",BODY,{"derivedFrom":makeQuery(id+"F9.opRevolve","SWEPT_BODY",BODY,{"disambiguationData":[OSD([sQuery(id+"F7.wireOp",EDGE,"E83.MirrorCS"),sQuery(id+"F7.wireOp",EDGE,"E84.MirrorCS"),sQuery(id+"F7.wireOp",EDGE,"E85.MirrorCS"),sQuery(id+"F7.wireOp",EDGE,"E86.MirrorCS")])]}),"instanceName":"1"}),"instanceName":"1"}),"instanceName":"1"}),"instanceName":"1"});
            var Q5;
            Q5=sQuery(id+"F0.wireOp",EDGE,"E22");
            transform(context, id + "F15", {"entities" : qUnion([Q0, Q1, Q2, Q3, Q4]), "transformType" : TransformType.TRANSLATION_ENTITY, "oppositeDirectionEntity" : false, "transformLine" : qUnion([Q5]), "makeCopy" : true});
        }
        {
            var Q0;
            Q0=makeQuery(id+"F15.opPattern","COPY",BODY,{"derivedFrom":makeQuery(id+"F14.opPattern","COPY",BODY,{"derivedFrom":makeQuery(id+"F13.opPattern","COPY",BODY,{"derivedFrom":makeQuery(id+"F12.opPattern","COPY",BODY,{"derivedFrom":makeQuery(id+"F10.opPattern","COPY",BODY,{"derivedFrom":makeQuery(id+"F9.opRevolve","SWEPT_BODY",BODY,{"disambiguationData":[OSD([sQuery(id+"F7.wireOp",EDGE,"E83.MirrorCS"),sQuery(id+"F7.wireOp",EDGE,"E84.MirrorCS"),sQuery(id+"F7.wireOp",EDGE,"E85.MirrorCS"),sQuery(id+"F7.wireOp",EDGE,"E86.MirrorCS")])]}),"instanceName":"1"}),"instanceName":"1"}),"instanceName":"1"}),"instanceName":"1"}),"instanceName":"1"});
            var Q1;
            Q1=makeQuery(id+"F15.opPattern","COPY",BODY,{"derivedFrom":makeQuery(id+"F14.opPattern","COPY",BODY,{"derivedFrom":makeQuery(id+"F13.opPattern","COPY",BODY,{"derivedFrom":makeQuery(id+"F12.opPattern","COPY",BODY,{"derivedFrom":makeQuery(id+"F10.opPattern","COPY",BODY,{"derivedFrom":makeQuery(id+"F6.opRevolve","SWEPT_BODY",BODY,{"disambiguationData":[OSD([sQuery(id+"F5.wireOp",EDGE,"E66.bottom"),sQuery(id+"F5.wireOp",EDGE,"E66.top"),sQuery(id+"F5.wireOp",EDGE,"E66.left"),sQuery(id+"F5.wireOp",EDGE,"E66.right"),sQuery(id+"F5.wireOp",EDGE,"E67.bottom"),sQuery(id+"F5.wireOp",EDGE,"E67.top"),sQuery(id+"F5.wireOp",EDGE,"E67.right")])]}),"instanceName":"1"}),"instanceName":"1"}),"instanceName":"1"}),"instanceName":"1"}),"instanceName":"1"});
            var Q2;
            Q2=makeQuery(id+"F15.opPattern","COPY",BODY,{"derivedFrom":makeQuery(id+"F14.opPattern","COPY",BODY,{"derivedFrom":makeQuery(id+"F13.opPattern","COPY",BODY,{"derivedFrom":makeQuery(id+"F12.opPattern","COPY",BODY,{"derivedFrom":makeQuery(id+"F10.opPattern","COPY",BODY,{"derivedFrom":makeQuery(id+"F6.opRevolve","SWEPT_BODY",BODY,{"disambiguationData":[OSD([sQuery(id+"F5.wireOp",EDGE,"E70.MirrorCS"),sQuery(id+"F5.wireOp",EDGE,"E71.MirrorCS"),sQuery(id+"F5.wireOp",EDGE,"E72.MirrorCS"),sQuery(id+"F5.wireOp",EDGE,"E74.MirrorCS"),sQuery(id+"F5.wireOp",EDGE,"E75.MirrorCS"),sQuery(id+"F5.wireOp",EDGE,"E76.MirrorCS"),sQuery(id+"F5.wireOp",EDGE,"E77.MirrorCS")])]}),"instanceName":"1"}),"instanceName":"1"}),"instanceName":"1"}),"instanceName":"1"}),"instanceName":"1"});
            var Q3;
            Q3=makeQuery(id+"F15.opPattern","COPY",BODY,{"derivedFrom":makeQuery(id+"F14.opPattern","COPY",BODY,{"derivedFrom":makeQuery(id+"F13.opPattern","COPY",BODY,{"derivedFrom":makeQuery(id+"F12.opPattern","COPY",BODY,{"derivedFrom":makeQuery(id+"F10.opPattern","COPY",BODY,{"derivedFrom":makeQuery(id+"F8.opRevolve","SWEPT_BODY",BODY,{"disambiguationData":[OSD([sQuery(id+"F7.wireOp",EDGE,"E81.bottom"),sQuery(id+"F7.wireOp",EDGE,"E81.top"),sQuery(id+"F7.wireOp",EDGE,"E81.left"),sQuery(id+"F7.wireOp",EDGE,"E81.right")])]}),"instanceName":"1"}),"instanceName":"1"}),"instanceName":"1"}),"instanceName":"1"}),"instanceName":"1"});
            var Q4;
            Q4=makeQuery(id+"F15.opPattern","COPY",BODY,{"derivedFrom":makeQuery(id+"F14.opPattern","COPY",BODY,{"derivedFrom":makeQuery(id+"F13.opPattern","COPY",BODY,{"derivedFrom":makeQuery(id+"F12.opPattern","COPY",BODY,{"derivedFrom":makeQuery(id+"F10.opPattern","COPY",BODY,{"derivedFrom":makeQuery(id+"F4.opRevolve","SWEPT_BODY",BODY,{"disambiguationData":[OSD([sQuery(id+"F3.wireOp",EDGE,"E57.6"),sQuery(id+"F3.wireOp",EDGE,"E58.0"),sQuery(id+"F3.wireOp",EDGE,"E62"),sQuery(id+"F3.wireOp",EDGE,"E63")])]}),"instanceName":"1"}),"instanceName":"1"}),"instanceName":"1"}),"instanceName":"1"}),"instanceName":"1"});
            var Q5;
            Q5=sQuery(id+"F0.wireOp",EDGE,"E44");
            transform(context, id + "F16", {"entities" : qUnion([Q0, Q1, Q2, Q3, Q4]), "transformType" : TransformType.TRANSLATION_ENTITY, "oppositeDirectionEntity" : true, "transformLine" : qUnion([Q5]), "makeCopy" : false});
        }
        {
            var Q0;
            Q0=makeQuery(id+"F15.opPattern","COPY",BODY,{"derivedFrom":makeQuery(id+"F14.opPattern","COPY",BODY,{"derivedFrom":makeQuery(id+"F13.opPattern","COPY",BODY,{"derivedFrom":makeQuery(id+"F12.opPattern","COPY",BODY,{"derivedFrom":makeQuery(id+"F10.opPattern","COPY",BODY,{"derivedFrom":makeQuery(id+"F4.opRevolve","SWEPT_BODY",BODY,{"disambiguationData":[OSD([sQuery(id+"F3.wireOp",EDGE,"E57.6"),sQuery(id+"F3.wireOp",EDGE,"E58.0"),sQuery(id+"F3.wireOp",EDGE,"E62"),sQuery(id+"F3.wireOp",EDGE,"E63")])]}),"instanceName":"1"}),"instanceName":"1"}),"instanceName":"1"}),"instanceName":"1"}),"instanceName":"1"});
            var Q1;
            Q1=makeQuery(id+"F15.opPattern","COPY",BODY,{"derivedFrom":makeQuery(id+"F14.opPattern","COPY",BODY,{"derivedFrom":makeQuery(id+"F13.opPattern","COPY",BODY,{"derivedFrom":makeQuery(id+"F12.opPattern","COPY",BODY,{"derivedFrom":makeQuery(id+"F10.opPattern","COPY",BODY,{"derivedFrom":makeQuery(id+"F6.opRevolve","SWEPT_BODY",BODY,{"disambiguationData":[OSD([sQuery(id+"F5.wireOp",EDGE,"E66.bottom"),sQuery(id+"F5.wireOp",EDGE,"E66.top"),sQuery(id+"F5.wireOp",EDGE,"E66.left"),sQuery(id+"F5.wireOp",EDGE,"E66.right"),sQuery(id+"F5.wireOp",EDGE,"E67.bottom"),sQuery(id+"F5.wireOp",EDGE,"E67.top"),sQuery(id+"F5.wireOp",EDGE,"E67.right")])]}),"instanceName":"1"}),"instanceName":"1"}),"instanceName":"1"}),"instanceName":"1"}),"instanceName":"1"});
            var Q2;
            Q2=makeQuery(id+"F15.opPattern","COPY",BODY,{"derivedFrom":makeQuery(id+"F14.opPattern","COPY",BODY,{"derivedFrom":makeQuery(id+"F13.opPattern","COPY",BODY,{"derivedFrom":makeQuery(id+"F12.opPattern","COPY",BODY,{"derivedFrom":makeQuery(id+"F10.opPattern","COPY",BODY,{"derivedFrom":makeQuery(id+"F6.opRevolve","SWEPT_BODY",BODY,{"disambiguationData":[OSD([sQuery(id+"F5.wireOp",EDGE,"E70.MirrorCS"),sQuery(id+"F5.wireOp",EDGE,"E71.MirrorCS"),sQuery(id+"F5.wireOp",EDGE,"E72.MirrorCS"),sQuery(id+"F5.wireOp",EDGE,"E74.MirrorCS"),sQuery(id+"F5.wireOp",EDGE,"E75.MirrorCS"),sQuery(id+"F5.wireOp",EDGE,"E76.MirrorCS"),sQuery(id+"F5.wireOp",EDGE,"E77.MirrorCS")])]}),"instanceName":"1"}),"instanceName":"1"}),"instanceName":"1"}),"instanceName":"1"}),"instanceName":"1"});
            var Q3;
            Q3=makeQuery(id+"F15.opPattern","COPY",BODY,{"derivedFrom":makeQuery(id+"F14.opPattern","COPY",BODY,{"derivedFrom":makeQuery(id+"F13.opPattern","COPY",BODY,{"derivedFrom":makeQuery(id+"F12.opPattern","COPY",BODY,{"derivedFrom":makeQuery(id+"F10.opPattern","COPY",BODY,{"derivedFrom":makeQuery(id+"F8.opRevolve","SWEPT_BODY",BODY,{"disambiguationData":[OSD([sQuery(id+"F7.wireOp",EDGE,"E81.bottom"),sQuery(id+"F7.wireOp",EDGE,"E81.top"),sQuery(id+"F7.wireOp",EDGE,"E81.left"),sQuery(id+"F7.wireOp",EDGE,"E81.right")])]}),"instanceName":"1"}),"instanceName":"1"}),"instanceName":"1"}),"instanceName":"1"}),"instanceName":"1"});
            var Q4;
            Q4=makeQuery(id+"F15.opPattern","COPY",BODY,{"derivedFrom":makeQuery(id+"F14.opPattern","COPY",BODY,{"derivedFrom":makeQuery(id+"F13.opPattern","COPY",BODY,{"derivedFrom":makeQuery(id+"F12.opPattern","COPY",BODY,{"derivedFrom":makeQuery(id+"F10.opPattern","COPY",BODY,{"derivedFrom":makeQuery(id+"F9.opRevolve","SWEPT_BODY",BODY,{"disambiguationData":[OSD([sQuery(id+"F7.wireOp",EDGE,"E83.MirrorCS"),sQuery(id+"F7.wireOp",EDGE,"E84.MirrorCS"),sQuery(id+"F7.wireOp",EDGE,"E85.MirrorCS"),sQuery(id+"F7.wireOp",EDGE,"E86.MirrorCS")])]}),"instanceName":"1"}),"instanceName":"1"}),"instanceName":"1"}),"instanceName":"1"}),"instanceName":"1"});
            var Q5;
            Q5=sQuery(id+"F0.wireOp",EDGE,"E52");
            transform(context, id + "F17", {"entities" : qUnion([Q0, Q1, Q2, Q3, Q4]), "transformType" : TransformType.TRANSLATION_ENTITY, "oppositeDirectionEntity" : false, "transformLine" : qUnion([Q5]), "makeCopy" : true});
        }
        {
            var Q0;
            Q0=makeQuery(id+"F17.opPattern","COPY",BODY,{"derivedFrom":makeQuery(id+"F15.opPattern","COPY",BODY,{"derivedFrom":makeQuery(id+"F14.opPattern","COPY",BODY,{"derivedFrom":makeQuery(id+"F13.opPattern","COPY",BODY,{"derivedFrom":makeQuery(id+"F12.opPattern","COPY",BODY,{"derivedFrom":makeQuery(id+"F10.opPattern","COPY",BODY,{"derivedFrom":makeQuery(id+"F4.opRevolve","SWEPT_BODY",BODY,{"disambiguationData":[OSD([sQuery(id+"F3.wireOp",EDGE,"E57.6"),sQuery(id+"F3.wireOp",EDGE,"E58.0"),sQuery(id+"F3.wireOp",EDGE,"E62"),sQuery(id+"F3.wireOp",EDGE,"E63")])]}),"instanceName":"1"}),"instanceName":"1"}),"instanceName":"1"}),"instanceName":"1"}),"instanceName":"1"}),"instanceName":"1"});
            var Q1;
            Q1=makeQuery(id+"F17.opPattern","COPY",BODY,{"derivedFrom":makeQuery(id+"F15.opPattern","COPY",BODY,{"derivedFrom":makeQuery(id+"F14.opPattern","COPY",BODY,{"derivedFrom":makeQuery(id+"F13.opPattern","COPY",BODY,{"derivedFrom":makeQuery(id+"F12.opPattern","COPY",BODY,{"derivedFrom":makeQuery(id+"F10.opPattern","COPY",BODY,{"derivedFrom":makeQuery(id+"F6.opRevolve","SWEPT_BODY",BODY,{"disambiguationData":[OSD([sQuery(id+"F5.wireOp",EDGE,"E66.bottom"),sQuery(id+"F5.wireOp",EDGE,"E66.top"),sQuery(id+"F5.wireOp",EDGE,"E66.left"),sQuery(id+"F5.wireOp",EDGE,"E66.right"),sQuery(id+"F5.wireOp",EDGE,"E67.bottom"),sQuery(id+"F5.wireOp",EDGE,"E67.top"),sQuery(id+"F5.wireOp",EDGE,"E67.right")])]}),"instanceName":"1"}),"instanceName":"1"}),"instanceName":"1"}),"instanceName":"1"}),"instanceName":"1"}),"instanceName":"1"});
            var Q2;
            Q2=makeQuery(id+"F17.opPattern","COPY",BODY,{"derivedFrom":makeQuery(id+"F15.opPattern","COPY",BODY,{"derivedFrom":makeQuery(id+"F14.opPattern","COPY",BODY,{"derivedFrom":makeQuery(id+"F13.opPattern","COPY",BODY,{"derivedFrom":makeQuery(id+"F12.opPattern","COPY",BODY,{"derivedFrom":makeQuery(id+"F10.opPattern","COPY",BODY,{"derivedFrom":makeQuery(id+"F6.opRevolve","SWEPT_BODY",BODY,{"disambiguationData":[OSD([sQuery(id+"F5.wireOp",EDGE,"E70.MirrorCS"),sQuery(id+"F5.wireOp",EDGE,"E71.MirrorCS"),sQuery(id+"F5.wireOp",EDGE,"E72.MirrorCS"),sQuery(id+"F5.wireOp",EDGE,"E74.MirrorCS"),sQuery(id+"F5.wireOp",EDGE,"E75.MirrorCS"),sQuery(id+"F5.wireOp",EDGE,"E76.MirrorCS"),sQuery(id+"F5.wireOp",EDGE,"E77.MirrorCS")])]}),"instanceName":"1"}),"instanceName":"1"}),"instanceName":"1"}),"instanceName":"1"}),"instanceName":"1"}),"instanceName":"1"});
            var Q3;
            Q3=makeQuery(id+"F17.opPattern","COPY",BODY,{"derivedFrom":makeQuery(id+"F15.opPattern","COPY",BODY,{"derivedFrom":makeQuery(id+"F14.opPattern","COPY",BODY,{"derivedFrom":makeQuery(id+"F13.opPattern","COPY",BODY,{"derivedFrom":makeQuery(id+"F12.opPattern","COPY",BODY,{"derivedFrom":makeQuery(id+"F10.opPattern","COPY",BODY,{"derivedFrom":makeQuery(id+"F8.opRevolve","SWEPT_BODY",BODY,{"disambiguationData":[OSD([sQuery(id+"F7.wireOp",EDGE,"E81.bottom"),sQuery(id+"F7.wireOp",EDGE,"E81.top"),sQuery(id+"F7.wireOp",EDGE,"E81.left"),sQuery(id+"F7.wireOp",EDGE,"E81.right")])]}),"instanceName":"1"}),"instanceName":"1"}),"instanceName":"1"}),"instanceName":"1"}),"instanceName":"1"}),"instanceName":"1"});
            var Q4;
            Q4=makeQuery(id+"F17.opPattern","COPY",BODY,{"derivedFrom":makeQuery(id+"F15.opPattern","COPY",BODY,{"derivedFrom":makeQuery(id+"F14.opPattern","COPY",BODY,{"derivedFrom":makeQuery(id+"F13.opPattern","COPY",BODY,{"derivedFrom":makeQuery(id+"F12.opPattern","COPY",BODY,{"derivedFrom":makeQuery(id+"F10.opPattern","COPY",BODY,{"derivedFrom":makeQuery(id+"F9.opRevolve","SWEPT_BODY",BODY,{"disambiguationData":[OSD([sQuery(id+"F7.wireOp",EDGE,"E83.MirrorCS"),sQuery(id+"F7.wireOp",EDGE,"E84.MirrorCS"),sQuery(id+"F7.wireOp",EDGE,"E85.MirrorCS"),sQuery(id+"F7.wireOp",EDGE,"E86.MirrorCS")])]}),"instanceName":"1"}),"instanceName":"1"}),"instanceName":"1"}),"instanceName":"1"}),"instanceName":"1"}),"instanceName":"1"});
            var Q5;
            Q5=sQuery(id+"F0.wireOp",EDGE,"E47");
            transform(context, id + "F18", {"entities" : qUnion([Q0, Q1, Q2, Q3, Q4]), "transformType" : TransformType.TRANSLATION_ENTITY, "oppositeDirectionEntity" : true, "transformLine" : qUnion([Q5]), "makeCopy" : false});
        }
        {
            var Q0;
            Q0=makeQuery(id+"F17.opPattern","COPY",BODY,{"derivedFrom":makeQuery(id+"F15.opPattern","COPY",BODY,{"derivedFrom":makeQuery(id+"F14.opPattern","COPY",BODY,{"derivedFrom":makeQuery(id+"F13.opPattern","COPY",BODY,{"derivedFrom":makeQuery(id+"F12.opPattern","COPY",BODY,{"derivedFrom":makeQuery(id+"F10.opPattern","COPY",BODY,{"derivedFrom":makeQuery(id+"F4.opRevolve","SWEPT_BODY",BODY,{"disambiguationData":[OSD([sQuery(id+"F3.wireOp",EDGE,"E57.6"),sQuery(id+"F3.wireOp",EDGE,"E58.0"),sQuery(id+"F3.wireOp",EDGE,"E62"),sQuery(id+"F3.wireOp",EDGE,"E63")])]}),"instanceName":"1"}),"instanceName":"1"}),"instanceName":"1"}),"instanceName":"1"}),"instanceName":"1"}),"instanceName":"1"});
            var Q1;
            Q1=makeQuery(id+"F17.opPattern","COPY",BODY,{"derivedFrom":makeQuery(id+"F15.opPattern","COPY",BODY,{"derivedFrom":makeQuery(id+"F14.opPattern","COPY",BODY,{"derivedFrom":makeQuery(id+"F13.opPattern","COPY",BODY,{"derivedFrom":makeQuery(id+"F12.opPattern","COPY",BODY,{"derivedFrom":makeQuery(id+"F10.opPattern","COPY",BODY,{"derivedFrom":makeQuery(id+"F6.opRevolve","SWEPT_BODY",BODY,{"disambiguationData":[OSD([sQuery(id+"F5.wireOp",EDGE,"E66.bottom"),sQuery(id+"F5.wireOp",EDGE,"E66.top"),sQuery(id+"F5.wireOp",EDGE,"E66.left"),sQuery(id+"F5.wireOp",EDGE,"E66.right"),sQuery(id+"F5.wireOp",EDGE,"E67.bottom"),sQuery(id+"F5.wireOp",EDGE,"E67.top"),sQuery(id+"F5.wireOp",EDGE,"E67.right")])]}),"instanceName":"1"}),"instanceName":"1"}),"instanceName":"1"}),"instanceName":"1"}),"instanceName":"1"}),"instanceName":"1"});
            var Q2;
            Q2=makeQuery(id+"F17.opPattern","COPY",BODY,{"derivedFrom":makeQuery(id+"F15.opPattern","COPY",BODY,{"derivedFrom":makeQuery(id+"F14.opPattern","COPY",BODY,{"derivedFrom":makeQuery(id+"F13.opPattern","COPY",BODY,{"derivedFrom":makeQuery(id+"F12.opPattern","COPY",BODY,{"derivedFrom":makeQuery(id+"F10.opPattern","COPY",BODY,{"derivedFrom":makeQuery(id+"F6.opRevolve","SWEPT_BODY",BODY,{"disambiguationData":[OSD([sQuery(id+"F5.wireOp",EDGE,"E70.MirrorCS"),sQuery(id+"F5.wireOp",EDGE,"E71.MirrorCS"),sQuery(id+"F5.wireOp",EDGE,"E72.MirrorCS"),sQuery(id+"F5.wireOp",EDGE,"E74.MirrorCS"),sQuery(id+"F5.wireOp",EDGE,"E75.MirrorCS"),sQuery(id+"F5.wireOp",EDGE,"E76.MirrorCS"),sQuery(id+"F5.wireOp",EDGE,"E77.MirrorCS")])]}),"instanceName":"1"}),"instanceName":"1"}),"instanceName":"1"}),"instanceName":"1"}),"instanceName":"1"}),"instanceName":"1"});
            var Q3;
            Q3=makeQuery(id+"F17.opPattern","COPY",BODY,{"derivedFrom":makeQuery(id+"F15.opPattern","COPY",BODY,{"derivedFrom":makeQuery(id+"F14.opPattern","COPY",BODY,{"derivedFrom":makeQuery(id+"F13.opPattern","COPY",BODY,{"derivedFrom":makeQuery(id+"F12.opPattern","COPY",BODY,{"derivedFrom":makeQuery(id+"F10.opPattern","COPY",BODY,{"derivedFrom":makeQuery(id+"F8.opRevolve","SWEPT_BODY",BODY,{"disambiguationData":[OSD([sQuery(id+"F7.wireOp",EDGE,"E81.bottom"),sQuery(id+"F7.wireOp",EDGE,"E81.top"),sQuery(id+"F7.wireOp",EDGE,"E81.left"),sQuery(id+"F7.wireOp",EDGE,"E81.right")])]}),"instanceName":"1"}),"instanceName":"1"}),"instanceName":"1"}),"instanceName":"1"}),"instanceName":"1"}),"instanceName":"1"});
            var Q4;
            Q4=makeQuery(id+"F17.opPattern","COPY",BODY,{"derivedFrom":makeQuery(id+"F15.opPattern","COPY",BODY,{"derivedFrom":makeQuery(id+"F14.opPattern","COPY",BODY,{"derivedFrom":makeQuery(id+"F13.opPattern","COPY",BODY,{"derivedFrom":makeQuery(id+"F12.opPattern","COPY",BODY,{"derivedFrom":makeQuery(id+"F10.opPattern","COPY",BODY,{"derivedFrom":makeQuery(id+"F9.opRevolve","SWEPT_BODY",BODY,{"disambiguationData":[OSD([sQuery(id+"F7.wireOp",EDGE,"E83.MirrorCS"),sQuery(id+"F7.wireOp",EDGE,"E84.MirrorCS"),sQuery(id+"F7.wireOp",EDGE,"E85.MirrorCS"),sQuery(id+"F7.wireOp",EDGE,"E86.MirrorCS")])]}),"instanceName":"1"}),"instanceName":"1"}),"instanceName":"1"}),"instanceName":"1"}),"instanceName":"1"}),"instanceName":"1"});
            var Q5;
            Q5=sQuery(id+"F0.wireOp",EDGE,"E53");
            transform(context, id + "F19", {"entities" : qUnion([Q0, Q1, Q2, Q3, Q4]), "transformType" : TransformType.TRANSLATION_ENTITY, "oppositeDirectionEntity" : false, "transformLine" : qUnion([Q5]), "makeCopy" : true});
        }
        {
            var Q0;
            Q0=makeQuery(id+"F19.opPattern","COPY",BODY,{"derivedFrom":makeQuery(id+"F17.opPattern","COPY",BODY,{"derivedFrom":makeQuery(id+"F15.opPattern","COPY",BODY,{"derivedFrom":makeQuery(id+"F14.opPattern","COPY",BODY,{"derivedFrom":makeQuery(id+"F13.opPattern","COPY",BODY,{"derivedFrom":makeQuery(id+"F12.opPattern","COPY",BODY,{"derivedFrom":makeQuery(id+"F10.opPattern","COPY",BODY,{"derivedFrom":makeQuery(id+"F6.opRevolve","SWEPT_BODY",BODY,{"disambiguationData":[OSD([sQuery(id+"F5.wireOp",EDGE,"E66.bottom"),sQuery(id+"F5.wireOp",EDGE,"E66.top"),sQuery(id+"F5.wireOp",EDGE,"E66.left"),sQuery(id+"F5.wireOp",EDGE,"E66.right"),sQuery(id+"F5.wireOp",EDGE,"E67.bottom"),sQuery(id+"F5.wireOp",EDGE,"E67.top"),sQuery(id+"F5.wireOp",EDGE,"E67.right")])]}),"instanceName":"1"}),"instanceName":"1"}),"instanceName":"1"}),"instanceName":"1"}),"instanceName":"1"}),"instanceName":"1"}),"instanceName":"1"});
            var Q1;
            Q1=makeQuery(id+"F19.opPattern","COPY",BODY,{"derivedFrom":makeQuery(id+"F17.opPattern","COPY",BODY,{"derivedFrom":makeQuery(id+"F15.opPattern","COPY",BODY,{"derivedFrom":makeQuery(id+"F14.opPattern","COPY",BODY,{"derivedFrom":makeQuery(id+"F13.opPattern","COPY",BODY,{"derivedFrom":makeQuery(id+"F12.opPattern","COPY",BODY,{"derivedFrom":makeQuery(id+"F10.opPattern","COPY",BODY,{"derivedFrom":makeQuery(id+"F4.opRevolve","SWEPT_BODY",BODY,{"disambiguationData":[OSD([sQuery(id+"F3.wireOp",EDGE,"E57.6"),sQuery(id+"F3.wireOp",EDGE,"E58.0"),sQuery(id+"F3.wireOp",EDGE,"E62"),sQuery(id+"F3.wireOp",EDGE,"E63")])]}),"instanceName":"1"}),"instanceName":"1"}),"instanceName":"1"}),"instanceName":"1"}),"instanceName":"1"}),"instanceName":"1"}),"instanceName":"1"});
            var Q2;
            Q2=makeQuery(id+"F19.opPattern","COPY",BODY,{"derivedFrom":makeQuery(id+"F17.opPattern","COPY",BODY,{"derivedFrom":makeQuery(id+"F15.opPattern","COPY",BODY,{"derivedFrom":makeQuery(id+"F14.opPattern","COPY",BODY,{"derivedFrom":makeQuery(id+"F13.opPattern","COPY",BODY,{"derivedFrom":makeQuery(id+"F12.opPattern","COPY",BODY,{"derivedFrom":makeQuery(id+"F10.opPattern","COPY",BODY,{"derivedFrom":makeQuery(id+"F6.opRevolve","SWEPT_BODY",BODY,{"disambiguationData":[OSD([sQuery(id+"F5.wireOp",EDGE,"E70.MirrorCS"),sQuery(id+"F5.wireOp",EDGE,"E71.MirrorCS"),sQuery(id+"F5.wireOp",EDGE,"E72.MirrorCS"),sQuery(id+"F5.wireOp",EDGE,"E74.MirrorCS"),sQuery(id+"F5.wireOp",EDGE,"E75.MirrorCS"),sQuery(id+"F5.wireOp",EDGE,"E76.MirrorCS"),sQuery(id+"F5.wireOp",EDGE,"E77.MirrorCS")])]}),"instanceName":"1"}),"instanceName":"1"}),"instanceName":"1"}),"instanceName":"1"}),"instanceName":"1"}),"instanceName":"1"}),"instanceName":"1"});
            var Q3;
            Q3=makeQuery(id+"F19.opPattern","COPY",BODY,{"derivedFrom":makeQuery(id+"F17.opPattern","COPY",BODY,{"derivedFrom":makeQuery(id+"F15.opPattern","COPY",BODY,{"derivedFrom":makeQuery(id+"F14.opPattern","COPY",BODY,{"derivedFrom":makeQuery(id+"F13.opPattern","COPY",BODY,{"derivedFrom":makeQuery(id+"F12.opPattern","COPY",BODY,{"derivedFrom":makeQuery(id+"F10.opPattern","COPY",BODY,{"derivedFrom":makeQuery(id+"F8.opRevolve","SWEPT_BODY",BODY,{"disambiguationData":[OSD([sQuery(id+"F7.wireOp",EDGE,"E81.bottom"),sQuery(id+"F7.wireOp",EDGE,"E81.top"),sQuery(id+"F7.wireOp",EDGE,"E81.left"),sQuery(id+"F7.wireOp",EDGE,"E81.right")])]}),"instanceName":"1"}),"instanceName":"1"}),"instanceName":"1"}),"instanceName":"1"}),"instanceName":"1"}),"instanceName":"1"}),"instanceName":"1"});
            var Q4;
            Q4=makeQuery(id+"F19.opPattern","COPY",BODY,{"derivedFrom":makeQuery(id+"F17.opPattern","COPY",BODY,{"derivedFrom":makeQuery(id+"F15.opPattern","COPY",BODY,{"derivedFrom":makeQuery(id+"F14.opPattern","COPY",BODY,{"derivedFrom":makeQuery(id+"F13.opPattern","COPY",BODY,{"derivedFrom":makeQuery(id+"F12.opPattern","COPY",BODY,{"derivedFrom":makeQuery(id+"F10.opPattern","COPY",BODY,{"derivedFrom":makeQuery(id+"F9.opRevolve","SWEPT_BODY",BODY,{"disambiguationData":[OSD([sQuery(id+"F7.wireOp",EDGE,"E83.MirrorCS"),sQuery(id+"F7.wireOp",EDGE,"E84.MirrorCS"),sQuery(id+"F7.wireOp",EDGE,"E85.MirrorCS"),sQuery(id+"F7.wireOp",EDGE,"E86.MirrorCS")])]}),"instanceName":"1"}),"instanceName":"1"}),"instanceName":"1"}),"instanceName":"1"}),"instanceName":"1"}),"instanceName":"1"}),"instanceName":"1"});
            var Q5;
            Q5=sQuery(id+"F0.wireOp",EDGE,"E48");
            transform(context, id + "F20", {"entities" : qUnion([Q0, Q1, Q2, Q3, Q4]), "transformType" : TransformType.TRANSLATION_ENTITY, "oppositeDirectionEntity" : true, "transformLine" : qUnion([Q5]), "makeCopy" : false});
        }
        {
            var Q0;
            Q0=makeQuery(id+"F13.opPattern","COPY",BODY,{"derivedFrom":makeQuery(id+"F12.opPattern","COPY",BODY,{"derivedFrom":makeQuery(id+"F10.opPattern","COPY",BODY,{"derivedFrom":makeQuery(id+"F4.opRevolve","SWEPT_BODY",BODY,{"disambiguationData":[OSD([sQuery(id+"F3.wireOp",EDGE,"E57.6"),sQuery(id+"F3.wireOp",EDGE,"E58.0"),sQuery(id+"F3.wireOp",EDGE,"E62"),sQuery(id+"F3.wireOp",EDGE,"E63")])]}),"instanceName":"1"}),"instanceName":"1"}),"instanceName":"1"});
            var Q1;
            Q1=makeQuery(id+"F13.opPattern","COPY",BODY,{"derivedFrom":makeQuery(id+"F12.opPattern","COPY",BODY,{"derivedFrom":makeQuery(id+"F10.opPattern","COPY",BODY,{"derivedFrom":makeQuery(id+"F9.opRevolve","SWEPT_BODY",BODY,{"disambiguationData":[OSD([sQuery(id+"F7.wireOp",EDGE,"E83.MirrorCS"),sQuery(id+"F7.wireOp",EDGE,"E84.MirrorCS"),sQuery(id+"F7.wireOp",EDGE,"E85.MirrorCS"),sQuery(id+"F7.wireOp",EDGE,"E86.MirrorCS")])]}),"instanceName":"1"}),"instanceName":"1"}),"instanceName":"1"});
            var Q2;
            Q2=makeQuery(id+"F13.opPattern","COPY",BODY,{"derivedFrom":makeQuery(id+"F12.opPattern","COPY",BODY,{"derivedFrom":makeQuery(id+"F10.opPattern","COPY",BODY,{"derivedFrom":makeQuery(id+"F8.opRevolve","SWEPT_BODY",BODY,{"disambiguationData":[OSD([sQuery(id+"F7.wireOp",EDGE,"E81.bottom"),sQuery(id+"F7.wireOp",EDGE,"E81.top"),sQuery(id+"F7.wireOp",EDGE,"E81.left"),sQuery(id+"F7.wireOp",EDGE,"E81.right")])]}),"instanceName":"1"}),"instanceName":"1"}),"instanceName":"1"});
            var Q3;
            Q3=makeQuery(id+"F13.opPattern","COPY",BODY,{"derivedFrom":makeQuery(id+"F12.opPattern","COPY",BODY,{"derivedFrom":makeQuery(id+"F10.opPattern","COPY",BODY,{"derivedFrom":makeQuery(id+"F6.opRevolve","SWEPT_BODY",BODY,{"disambiguationData":[OSD([sQuery(id+"F5.wireOp",EDGE,"E70.MirrorCS"),sQuery(id+"F5.wireOp",EDGE,"E71.MirrorCS"),sQuery(id+"F5.wireOp",EDGE,"E72.MirrorCS"),sQuery(id+"F5.wireOp",EDGE,"E74.MirrorCS"),sQuery(id+"F5.wireOp",EDGE,"E75.MirrorCS"),sQuery(id+"F5.wireOp",EDGE,"E76.MirrorCS"),sQuery(id+"F5.wireOp",EDGE,"E77.MirrorCS")])]}),"instanceName":"1"}),"instanceName":"1"}),"instanceName":"1"});
            var Q4;
            Q4=makeQuery(id+"F13.opPattern","COPY",BODY,{"derivedFrom":makeQuery(id+"F12.opPattern","COPY",BODY,{"derivedFrom":makeQuery(id+"F10.opPattern","COPY",BODY,{"derivedFrom":makeQuery(id+"F6.opRevolve","SWEPT_BODY",BODY,{"disambiguationData":[OSD([sQuery(id+"F5.wireOp",EDGE,"E66.bottom"),sQuery(id+"F5.wireOp",EDGE,"E66.top"),sQuery(id+"F5.wireOp",EDGE,"E66.left"),sQuery(id+"F5.wireOp",EDGE,"E66.right"),sQuery(id+"F5.wireOp",EDGE,"E67.bottom"),sQuery(id+"F5.wireOp",EDGE,"E67.top"),sQuery(id+"F5.wireOp",EDGE,"E67.right")])]}),"instanceName":"1"}),"instanceName":"1"}),"instanceName":"1"});
            deleteBodies(context, id + "F21", {"entities" : qUnion([Q0, Q1, Q2, Q3, Q4])});
        }
        {
            var Q0;
            Q0=qCreatedBy(makeId("Front.planeOp"),FACE);
            var sketch = newSketch(context, id + "F22", { "sketchPlane" : qUnion([Q0])});
            skArc(sketch, "E88.0", {"start": v(-1924.05, -789.93) * mm, "mid": v(-2006.15, -899.3) * mm, "end": v(-1905, -991.33) * mm});
            skArc(sketch, "E89.0", {"start": v(-1924.05, -791.55) * mm, "mid": v(-2004.55, -899.3) * mm, "end": v(-1905, -989.74) * mm});
            skLineSegment(sketch, "E90", {"start": v(-1905, -788.13) * mm, "end": v(-1905, -789.71) * mm, "construction": true});
            skLineSegment(sketch, "E91.trimOffspring", {"start": v(-1905, -889.73) * mm, "end": v(-1905, -989.74) * mm, "construction": true});
            skLineSegment(sketch, "E92.0", {"start": v(-1924.05, 1077.82) * mm, "end": v(-1924.05, -791.55) * mm, "construction": true});
            skLineSegment(sketch, "E93", {"start": v(-1924.05, -789.93) * mm, "end": v(-1924.05, -791.55) * mm});
            skLineSegment(sketch, "E94", {"start": v(-1905, -989.74) * mm, "end": v(-1905, -991.33) * mm});
            skSolve(sketch);
        }
        {
            var Q0;
            Q0 = qSketchRegion(id + "F22", true);
            var Q1;
            Q1=sQuery(id+"F22.wireOp",EDGE,"E91.trimOffspring");
            revolve(context, id + "F23", {"entities" : qUnion([Q0]), "axis" : qUnion([Q1]), "revolveType" : RevolveType.FULL});
        }
        {
            var Q0;
            Q0=qCreatedBy(makeId("Front.planeOp"),FACE);
            var sketch = newSketch(context, id + "F24", { "sketchPlane" : qUnion([Q0])});
            skLineSegment(sketch, "E95.0", {"start": v(-1924.05, -789.93) * mm, "end": v(-1885.95, -789.93) * mm, "construction": true});
            skCircle(sketch, "E96.0", {"center": v(-1905, -889.73) * mm, "radius": 101.6 * mm, "construction": true});
            skPoint(sketch, "E97.firstSnap0", {"position": v(-1905, -789.93) * mm});
            skLineSegment(sketch, "E97.bottom", {"start": v(-1905, -783.42) * mm, "end": v(-1930.4, -783.42) * mm});
            skLineSegment(sketch, "E97.top", {"start": v(-1905, -791.35) * mm, "end": v(-1930.4, -791.35) * mm});
            skLineSegment(sketch, "E97.left", {"start": v(-1905, -783.42) * mm, "end": v(-1905, -791.35) * mm});
            skLineSegment(sketch, "E97.right", {"start": v(-1930.4, -783.42) * mm, "end": v(-1930.4, -791.35) * mm});
            skSolve(sketch);
        }
        {
            var Q0;
            Q0=makeQuery(id+"F24.imprint","IMPRINT",FACE,{"disambiguationData":[TD([[makeQuery(id+"F24.imprint","IMPRINT",EDGE,{"derivedFrom":sQuery(id+"F24.wireOp",EDGE,"E97.bottom")}),1.0]])]});
            var Q1;
            Q1=sQuery(id+"F7.wireOp",EDGE,"E78.0");
            revolve(context, id + "F25", {"entities" : qUnion([Q0]), "axis" : qUnion([Q1]), "revolveType" : RevolveType.FULL});
        }
        {
            var Q0;
            Q0=makeQuery(id+"F23.opRevolve","SWEPT_BODY",BODY,{"disambiguationData":[OSD([sQuery(id+"F22.wireOp",EDGE,"E88.0"),sQuery(id+"F22.wireOp",EDGE,"E89.0"),sQuery(id+"F22.wireOp",EDGE,"f9vVGEoQ-YbhW-nNbm-u6YF-41upxqRHAMU5"),sQuery(id+"F22.wireOp",EDGE,"E93")])]});
            var Q1;
            Q1=makeQuery(id+"F25.opRevolve","SWEPT_BODY",BODY,{"disambiguationData":[OSD([sQuery(id+"F24.wireOp",EDGE,"E97.bottom"),sQuery(id+"F24.wireOp",EDGE,"E97.top"),sQuery(id+"F24.wireOp",EDGE,"E97.left"),sQuery(id+"F24.wireOp",EDGE,"E97.right")])]});
            var Q2;
            Q2=sQuery(id+"F0.wireOp",EDGE,"E35");
            transform(context, id + "F26", {"entities" : qUnion([Q0, Q1]), "transformType" : TransformType.TRANSLATION_ENTITY, "oppositeDirectionEntity" : true, "transformLine" : qUnion([Q2]), "makeCopy" : true});
        }
        {
            var Q0;
            Q0=makeQuery(id+"F26.opPattern","COPY",BODY,{"derivedFrom":makeQuery(id+"F23.opRevolve","SWEPT_BODY",BODY,{"disambiguationData":[OSD([sQuery(id+"F22.wireOp",EDGE,"E88.0"),sQuery(id+"F22.wireOp",EDGE,"E89.0"),sQuery(id+"F22.wireOp",EDGE,"f9vVGEoQ-YbhW-nNbm-u6YF-41upxqRHAMU5"),sQuery(id+"F22.wireOp",EDGE,"E93")])]}),"instanceName":"1"});
            var Q1;
            Q1=makeQuery(id+"F26.opPattern","COPY",BODY,{"derivedFrom":makeQuery(id+"F25.opRevolve","SWEPT_BODY",BODY,{"disambiguationData":[OSD([sQuery(id+"F24.wireOp",EDGE,"E97.bottom"),sQuery(id+"F24.wireOp",EDGE,"E97.top"),sQuery(id+"F24.wireOp",EDGE,"E97.left"),sQuery(id+"F24.wireOp",EDGE,"E97.right")])]}),"instanceName":"1"});
            var Q2;
            Q2=sQuery(id+"F0.wireOp",EDGE,"E54");
            transform(context, id + "F27", {"entities" : qUnion([Q0, Q1]), "transformType" : TransformType.TRANSLATION_ENTITY, "oppositeDirectionEntity" : false, "transformLine" : qUnion([Q2]), "makeCopy" : true});
        }
        {
            var Q0;
            Q0=makeQuery(id+"F27.opPattern","COPY",BODY,{"derivedFrom":makeQuery(id+"F26.opPattern","COPY",BODY,{"derivedFrom":makeQuery(id+"F25.opRevolve","SWEPT_BODY",BODY,{"disambiguationData":[OSD([sQuery(id+"F24.wireOp",EDGE,"E97.bottom"),sQuery(id+"F24.wireOp",EDGE,"E97.top"),sQuery(id+"F24.wireOp",EDGE,"E97.left"),sQuery(id+"F24.wireOp",EDGE,"E97.right")])]}),"instanceName":"1"}),"instanceName":"1"});
            var Q1;
            Q1=makeQuery(id+"F27.opPattern","COPY",BODY,{"derivedFrom":makeQuery(id+"F26.opPattern","COPY",BODY,{"derivedFrom":makeQuery(id+"F23.opRevolve","SWEPT_BODY",BODY,{"disambiguationData":[OSD([sQuery(id+"F22.wireOp",EDGE,"E88.0"),sQuery(id+"F22.wireOp",EDGE,"E89.0"),sQuery(id+"F22.wireOp",EDGE,"f9vVGEoQ-YbhW-nNbm-u6YF-41upxqRHAMU5"),sQuery(id+"F22.wireOp",EDGE,"E93")])]}),"instanceName":"1"}),"instanceName":"1"});
            var Q2;
            Q2=sQuery(id+"F0.wireOp",EDGE,"E55");
            transform(context, id + "F28", {"entities" : qUnion([Q0, Q1]), "transformType" : TransformType.TRANSLATION_ENTITY, "oppositeDirectionEntity" : true, "transformLine" : qUnion([Q2]), "makeCopy" : false});
        }
        {
            var Q0;
            Q0=qCreatedBy(makeId("Front.planeOp"),FACE);
            var sketch = newSketch(context, id + "F29", { "sketchPlane" : qUnion([Q0])});
            skLineSegment(sketch, "E98.0", {"start": v(-1625.6, 272.32) * mm, "end": v(-1104.9, 272.32) * mm});
            skLineSegment(sketch, "E98.1", {"start": v(-1651, 246.92) * mm, "end": v(-1079.5, 246.92) * mm, "construction": true});
            skLineSegment(sketch, "E99.top", {"start": v(-1625.6, 265.97) * mm, "end": v(-1104.9, 265.97) * mm});
            skLineSegment(sketch, "E99.left", {"start": v(-1625.6, 272.32) * mm, "end": v(-1625.6, 265.97) * mm});
            skLineSegment(sketch, "E99.right", {"start": v(-1104.9, 272.32) * mm, "end": v(-1104.9, 265.97) * mm});
            skLineSegment(sketch, "E100.bottom", {"start": v(-1625.6, 272.32) * mm, "end": v(-1633.54, 272.32) * mm});
            skLineSegment(sketch, "E100.top", {"start": v(-1625.6, 246.92) * mm, "end": v(-1633.54, 246.92) * mm});
            skLineSegment(sketch, "E100.left", {"start": v(-1625.6, 272.32) * mm, "end": v(-1625.6, 246.92) * mm});
            skLineSegment(sketch, "E100.right", {"start": v(-1633.54, 272.32) * mm, "end": v(-1633.54, 246.92) * mm});
            skLineSegment(sketch, "E101.bottom", {"start": v(-1651, 246.92) * mm, "end": v(-1633.54, 246.92) * mm});
            skLineSegment(sketch, "E101.top", {"start": v(-1651, 253.27) * mm, "end": v(-1633.54, 253.27) * mm});
            skLineSegment(sketch, "E101.left", {"start": v(-1651, 246.92) * mm, "end": v(-1651, 253.27) * mm});
            skLineSegment(sketch, "E101.right", {"start": v(-1633.54, 246.92) * mm, "end": v(-1633.54, 253.27) * mm});
            skLineSegment(sketch, "E102", {"start": v(-1365.25, 246.92) * mm, "end": v(-1365.25, 524.19) * mm, "construction": true});
            skLineSegment(sketch, "E103.MirrorCS", {"start": v(-1096.96, 246.92) * mm, "end": v(-1096.96, 253.27) * mm});
            skLineSegment(sketch, "E104.MirrorCS", {"start": v(-1104.9, 272.32) * mm, "end": v(-1096.96, 272.32) * mm});
            skLineSegment(sketch, "E105.MirrorCS", {"start": v(-1104.9, 272.32) * mm, "end": v(-1104.9, 246.92) * mm});
            skLineSegment(sketch, "E106.MirrorCS", {"start": v(-1079.5, 246.92) * mm, "end": v(-1079.5, 253.27) * mm});
            skLineSegment(sketch, "E107.MirrorCS", {"start": v(-1079.5, 253.27) * mm, "end": v(-1096.96, 253.27) * mm});
            skLineSegment(sketch, "E108.MirrorCS", {"start": v(-1079.5, 246.92) * mm, "end": v(-1096.96, 246.92) * mm});
            skLineSegment(sketch, "E109.MirrorCS", {"start": v(-1104.9, 246.92) * mm, "end": v(-1096.96, 246.92) * mm});
            skLineSegment(sketch, "E110.MirrorCS", {"start": v(-1096.96, 272.32) * mm, "end": v(-1096.96, 246.92) * mm});
            skSolve(sketch);
        }
        {
            var Q0;
            {var subQ0=sQuery(id+"F29.wireOp",EDGE,"E98.0");Q0=makeQuery(id+"F29.imprint","IMPRINT",FACE,{"disambiguationData":[TD([[makeQuery(id+"F29.imprint","IMPRINT",EDGE,{"derivedFrom":subQ0}),-1.0]])]});}
            var Q1;
            Q1=sQuery(id+"F29.wireOp",EDGE,"E98.1");
            revolve(context, id + "F30", {"entities" : qUnion([Q0]), "axis" : qUnion([Q1]), "revolveType" : RevolveType.FULL});
        }
        {
            var Q0;
            {var subQ3=sQuery(id+"F29.wireOp",EDGE,"E100.bottom");Q0=makeQuery(id+"F29.imprint","IMPRINT",FACE,{"disambiguationData":[TD([[makeQuery(id+"F29.imprint","IMPRINT",EDGE,{"derivedFrom":subQ3}),1.0]])]});}
            var Q1;
            Q1=makeQuery(id+"F29.imprint","IMPRINT",FACE,{"disambiguationData":[TD([[makeQuery(id+"F29.imprint","IMPRINT",EDGE,{"derivedFrom":sQuery(id+"F29.wireOp",EDGE,"E101.bottom")}),1.0]])]});
            var Q2;
            {var subQ3=sQuery(id+"F29.wireOp",EDGE,"E104.MirrorCS");Q2=makeQuery(id+"F29.imprint","IMPRINT",FACE,{"disambiguationData":[TD([[makeQuery(id+"F29.imprint","IMPRINT",EDGE,{"derivedFrom":subQ3}),-1.0]])]});}
            var Q3;
            Q3=makeQuery(id+"F29.imprint","IMPRINT",FACE,{"disambiguationData":[TD([[makeQuery(id+"F29.imprint","IMPRINT",EDGE,{"derivedFrom":sQuery(id+"F29.wireOp",EDGE,"E106.MirrorCS")}),1.0]])]});
            var Q4;
            Q4=sQuery(id+"F29.wireOp",EDGE,"E98.1");
            revolve(context, id + "F31", {"entities" : qUnion([Q0, Q1, Q2, Q3]), "axis" : qUnion([Q4]), "revolveType" : RevolveType.FULL});
        }
        {
            var Q0;
            Q0=qCreatedBy(makeId("Front.planeOp"),FACE);
            var sketch = newSketch(context, id + "F32", { "sketchPlane" : qUnion([Q0])});
            skLineSegment(sketch, "E111.1", {"start": v(-1651, 246.92) * mm, "end": v(-1633.54, 246.92) * mm, "construction": true});
            skLineSegment(sketch, "E111.2", {"start": v(-1365.25, 246.92) * mm, "end": v(-1365.25, 524.19) * mm, "construction": true});
            skLineSegment(sketch, "E112.bottom", {"start": v(-1651, 272.32) * mm, "end": v(-1658.94, 272.32) * mm});
            skLineSegment(sketch, "E112.top", {"start": v(-1651, 221.52) * mm, "end": v(-1658.94, 221.52) * mm});
            skLineSegment(sketch, "E112.left", {"start": v(-1651, 272.32) * mm, "end": v(-1651, 221.52) * mm});
            skLineSegment(sketch, "E112.right", {"start": v(-1658.94, 272.32) * mm, "end": v(-1658.94, 221.52) * mm});
            skPoint(sketch, "E113", {"position": v(-1651, 246.92) * mm});
            skPoint(sketch, "E114.MirrorP", {"position": v(-1079.5, 246.92) * mm});
            skLineSegment(sketch, "E115.MirrorCS", {"start": v(-1079.5, 272.32) * mm, "end": v(-1071.56, 272.32) * mm});
            skLineSegment(sketch, "E116.MirrorCS", {"start": v(-1079.5, 221.52) * mm, "end": v(-1071.56, 221.52) * mm});
            skLineSegment(sketch, "E117.MirrorCS", {"start": v(-1079.5, 272.32) * mm, "end": v(-1079.5, 221.52) * mm});
            skLineSegment(sketch, "E118.MirrorCS", {"start": v(-1071.56, 272.32) * mm, "end": v(-1071.56, 221.52) * mm});
            skSolve(sketch);
        }
        {
            var Q0;
            Q0=makeQuery(id+"F32.imprint","IMPRINT",FACE,{"disambiguationData":[TD([[makeQuery(id+"F32.imprint","IMPRINT",EDGE,{"derivedFrom":sQuery(id+"F32.wireOp",EDGE,"E112.bottom")}),1.0]])]});
            var Q1;
            Q1=sQuery(id+"F0.wireOp",EDGE,"E4");
            revolve(context, id + "F33", {"entities" : qUnion([Q0]), "axis" : qUnion([Q1]), "revolveType" : RevolveType.FULL});
        }
        {
            var Q0;
            Q0=makeQuery(id+"F32.imprint","IMPRINT",FACE,{"disambiguationData":[TD([[makeQuery(id+"F32.imprint","IMPRINT",EDGE,{"derivedFrom":sQuery(id+"F32.wireOp",EDGE,"E115.MirrorCS")}),-1.0]])]});
            var Q1;
            Q1=sQuery(id+"F0.wireOp",EDGE,"E5");
            revolve(context, id + "F34", {"entities" : qUnion([Q0]), "axis" : qUnion([Q1]), "revolveType" : RevolveType.FULL});
        }
        {
            var Q0;
            Q0=qCreatedBy(makeId("Front.planeOp"),FACE);
            var sketch = newSketch(context, id + "F35", { "sketchPlane" : qUnion([Q0])});
            skLineSegment(sketch, "E119.0", {"start": v(-1651, 246.92) * mm, "end": v(-1079.5, 246.92) * mm, "construction": true});
            skLineSegment(sketch, "E119.1", {"start": v(-825.5, -483.33) * mm, "end": v(-254, -483.33) * mm, "construction": true});
            skLineSegment(sketch, "E119.2", {"start": v(254, -45.18) * mm, "end": v(825.5, -45.18) * mm, "construction": true});
            skLineSegment(sketch, "E119.3", {"start": v(1079.5, -483.33) * mm, "end": v(1651, -483.33) * mm, "construction": true});
            skLineSegment(sketch, "E120", {"start": v(-1365.25, 373.25) * mm, "end": v(-539.75, 373.25) * mm, "construction": true});
            skPoint(sketch, "E120.startSnap0", {"position": v(-1365.25, 246.92) * mm});
            skPoint(sketch, "E120.endSnap0", {"position": v(-539.75, -483.33) * mm});
            skLineSegment(sketch, "E121", {"start": v(-539.75, 373.25) * mm, "end": v(539.75, 373.25) * mm, "construction": true});
            skPoint(sketch, "E121.endSnap0", {"position": v(539.75, -45.18) * mm});
            skLineSegment(sketch, "E122", {"start": v(539.75, 373.25) * mm, "end": v(1365.25, 373.25) * mm, "construction": true});
            skPoint(sketch, "E122.endSnap0", {"position": v(1365.25, -483.33) * mm});
            skLineSegment(sketch, "E123", {"start": v(-539.75, 246.92) * mm, "end": v(-539.75, -483.33) * mm, "construction": true});
            skLineSegment(sketch, "E124", {"start": v(539.75, -45.18) * mm, "end": v(539.75, -483.33) * mm, "construction": true});
            skLineSegment(sketch, "E125", {"start": v(1365.25, -483.33) * mm, "end": v(1365.25, -45.18) * mm, "construction": true});
            skSolve(sketch);
        }
        {
            var Q0;
            Q0=makeQuery(id+"F33.opRevolve","SWEPT_BODY",BODY,{"disambiguationData":[OSD([sQuery(id+"F32.wireOp",EDGE,"E112.bottom"),sQuery(id+"F32.wireOp",EDGE,"E112.top"),sQuery(id+"F32.wireOp",EDGE,"E112.left"),sQuery(id+"F32.wireOp",EDGE,"E112.right")])]});
            var Q1;
            Q1=makeQuery(id+"F31.opRevolve","SWEPT_BODY",BODY,{"disambiguationData":[OSD([sQuery(id+"F29.wireOp",EDGE,"E100.bottom"),sQuery(id+"F29.wireOp",EDGE,"E100.top"),sQuery(id+"F29.wireOp",EDGE,"E100.left"),sQuery(id+"F29.wireOp",EDGE,"E100.right"),sQuery(id+"F29.wireOp",EDGE,"E101.bottom"),sQuery(id+"F29.wireOp",EDGE,"E101.top"),sQuery(id+"F29.wireOp",EDGE,"E101.left")])]});
            var Q2;
            Q2=makeQuery(id+"F30.opRevolve","SWEPT_BODY",BODY,{"disambiguationData":[OSD([sQuery(id+"F29.wireOp",EDGE,"E98.0"),sQuery(id+"F29.wireOp",EDGE,"E99.top"),sQuery(id+"F29.wireOp",EDGE,"E100.left"),sQuery(id+"F29.wireOp",EDGE,"E105.MirrorCS")])]});
            var Q3;
            Q3=makeQuery(id+"F31.opRevolve","SWEPT_BODY",BODY,{"disambiguationData":[OSD([sQuery(id+"F29.wireOp",EDGE,"E104.MirrorCS"),sQuery(id+"F29.wireOp",EDGE,"E105.MirrorCS"),sQuery(id+"F29.wireOp",EDGE,"E106.MirrorCS"),sQuery(id+"F29.wireOp",EDGE,"E107.MirrorCS"),sQuery(id+"F29.wireOp",EDGE,"E108.MirrorCS"),sQuery(id+"F29.wireOp",EDGE,"E109.MirrorCS"),sQuery(id+"F29.wireOp",EDGE,"E110.MirrorCS")])]});
            var Q4;
            Q4=makeQuery(id+"F34.opRevolve","SWEPT_BODY",BODY,{"disambiguationData":[OSD([sQuery(id+"F32.wireOp",EDGE,"E115.MirrorCS"),sQuery(id+"F32.wireOp",EDGE,"E116.MirrorCS"),sQuery(id+"F32.wireOp",EDGE,"E117.MirrorCS"),sQuery(id+"F32.wireOp",EDGE,"E118.MirrorCS")])]});
            var Q5;
            Q5=sQuery(id+"F35.wireOp",EDGE,"E120");
            transform(context, id + "F36", {"entities" : qUnion([Q0, Q1, Q2, Q3, Q4]), "transformType" : TransformType.TRANSLATION_ENTITY, "oppositeDirectionEntity" : false, "transformLine" : qUnion([Q5]), "makeCopy" : true});
        }
        {
            var Q0;
            Q0=makeQuery(id+"F36.opPattern","COPY",BODY,{"derivedFrom":makeQuery(id+"F33.opRevolve","SWEPT_BODY",BODY,{"disambiguationData":[OSD([sQuery(id+"F32.wireOp",EDGE,"E112.bottom"),sQuery(id+"F32.wireOp",EDGE,"E112.top"),sQuery(id+"F32.wireOp",EDGE,"E112.left"),sQuery(id+"F32.wireOp",EDGE,"E112.right")])]}),"instanceName":"1"});
            var Q1;
            Q1=makeQuery(id+"F36.opPattern","COPY",BODY,{"derivedFrom":makeQuery(id+"F34.opRevolve","SWEPT_BODY",BODY,{"disambiguationData":[OSD([sQuery(id+"F32.wireOp",EDGE,"E115.MirrorCS"),sQuery(id+"F32.wireOp",EDGE,"E116.MirrorCS"),sQuery(id+"F32.wireOp",EDGE,"E117.MirrorCS"),sQuery(id+"F32.wireOp",EDGE,"E118.MirrorCS")])]}),"instanceName":"1"});
            var Q2;
            Q2=makeQuery(id+"F36.opPattern","COPY",BODY,{"derivedFrom":makeQuery(id+"F31.opRevolve","SWEPT_BODY",BODY,{"disambiguationData":[OSD([sQuery(id+"F29.wireOp",EDGE,"E100.bottom"),sQuery(id+"F29.wireOp",EDGE,"E100.top"),sQuery(id+"F29.wireOp",EDGE,"E100.left"),sQuery(id+"F29.wireOp",EDGE,"E100.right"),sQuery(id+"F29.wireOp",EDGE,"E101.bottom"),sQuery(id+"F29.wireOp",EDGE,"E101.top"),sQuery(id+"F29.wireOp",EDGE,"E101.left")])]}),"instanceName":"1"});
            var Q3;
            Q3=makeQuery(id+"F36.opPattern","COPY",BODY,{"derivedFrom":makeQuery(id+"F30.opRevolve","SWEPT_BODY",BODY,{"disambiguationData":[OSD([sQuery(id+"F29.wireOp",EDGE,"E98.0"),sQuery(id+"F29.wireOp",EDGE,"E99.top"),sQuery(id+"F29.wireOp",EDGE,"E100.left"),sQuery(id+"F29.wireOp",EDGE,"E105.MirrorCS")])]}),"instanceName":"1"});
            var Q4;
            Q4=makeQuery(id+"F36.opPattern","COPY",BODY,{"derivedFrom":makeQuery(id+"F31.opRevolve","SWEPT_BODY",BODY,{"disambiguationData":[OSD([sQuery(id+"F29.wireOp",EDGE,"E104.MirrorCS"),sQuery(id+"F29.wireOp",EDGE,"E105.MirrorCS"),sQuery(id+"F29.wireOp",EDGE,"E106.MirrorCS"),sQuery(id+"F29.wireOp",EDGE,"E107.MirrorCS"),sQuery(id+"F29.wireOp",EDGE,"E108.MirrorCS"),sQuery(id+"F29.wireOp",EDGE,"E109.MirrorCS"),sQuery(id+"F29.wireOp",EDGE,"E110.MirrorCS")])]}),"instanceName":"1"});
            var Q5;
            Q5=sQuery(id+"F35.wireOp",EDGE,"E123");
            transform(context, id + "F37", {"entities" : qUnion([Q0, Q1, Q2, Q3, Q4]), "transformType" : TransformType.TRANSLATION_ENTITY, "oppositeDirectionEntity" : false, "transformLine" : qUnion([Q5]), "makeCopy" : false});
        }
        {
            var Q0;
            Q0=makeQuery(id+"F36.opPattern","COPY",BODY,{"derivedFrom":makeQuery(id+"F33.opRevolve","SWEPT_BODY",BODY,{"disambiguationData":[OSD([sQuery(id+"F32.wireOp",EDGE,"E112.bottom"),sQuery(id+"F32.wireOp",EDGE,"E112.top"),sQuery(id+"F32.wireOp",EDGE,"E112.left"),sQuery(id+"F32.wireOp",EDGE,"E112.right")])]}),"instanceName":"1"});
            var Q1;
            Q1=makeQuery(id+"F36.opPattern","COPY",BODY,{"derivedFrom":makeQuery(id+"F34.opRevolve","SWEPT_BODY",BODY,{"disambiguationData":[OSD([sQuery(id+"F32.wireOp",EDGE,"E115.MirrorCS"),sQuery(id+"F32.wireOp",EDGE,"E116.MirrorCS"),sQuery(id+"F32.wireOp",EDGE,"E117.MirrorCS"),sQuery(id+"F32.wireOp",EDGE,"E118.MirrorCS")])]}),"instanceName":"1"});
            var Q2;
            Q2=makeQuery(id+"F36.opPattern","COPY",BODY,{"derivedFrom":makeQuery(id+"F31.opRevolve","SWEPT_BODY",BODY,{"disambiguationData":[OSD([sQuery(id+"F29.wireOp",EDGE,"E100.bottom"),sQuery(id+"F29.wireOp",EDGE,"E100.top"),sQuery(id+"F29.wireOp",EDGE,"E100.left"),sQuery(id+"F29.wireOp",EDGE,"E100.right"),sQuery(id+"F29.wireOp",EDGE,"E101.bottom"),sQuery(id+"F29.wireOp",EDGE,"E101.top"),sQuery(id+"F29.wireOp",EDGE,"E101.left")])]}),"instanceName":"1"});
            var Q3;
            Q3=makeQuery(id+"F36.opPattern","COPY",BODY,{"derivedFrom":makeQuery(id+"F30.opRevolve","SWEPT_BODY",BODY,{"disambiguationData":[OSD([sQuery(id+"F29.wireOp",EDGE,"E98.0"),sQuery(id+"F29.wireOp",EDGE,"E99.top"),sQuery(id+"F29.wireOp",EDGE,"E100.left"),sQuery(id+"F29.wireOp",EDGE,"E105.MirrorCS")])]}),"instanceName":"1"});
            var Q4;
            Q4=makeQuery(id+"F36.opPattern","COPY",BODY,{"derivedFrom":makeQuery(id+"F31.opRevolve","SWEPT_BODY",BODY,{"disambiguationData":[OSD([sQuery(id+"F29.wireOp",EDGE,"E104.MirrorCS"),sQuery(id+"F29.wireOp",EDGE,"E105.MirrorCS"),sQuery(id+"F29.wireOp",EDGE,"E106.MirrorCS"),sQuery(id+"F29.wireOp",EDGE,"E107.MirrorCS"),sQuery(id+"F29.wireOp",EDGE,"E108.MirrorCS"),sQuery(id+"F29.wireOp",EDGE,"E109.MirrorCS"),sQuery(id+"F29.wireOp",EDGE,"E110.MirrorCS")])]}),"instanceName":"1"});
            var Q5;
            Q5=sQuery(id+"F35.wireOp",EDGE,"E121");
            transform(context, id + "F38", {"entities" : qUnion([Q0, Q1, Q2, Q3, Q4]), "transformType" : TransformType.TRANSLATION_ENTITY, "oppositeDirectionEntity" : false, "transformLine" : qUnion([Q5]), "makeCopy" : true});
        }
        {
            var Q0;
            Q0=makeQuery(id+"F38.opPattern","COPY",BODY,{"derivedFrom":makeQuery(id+"F36.opPattern","COPY",BODY,{"derivedFrom":makeQuery(id+"F33.opRevolve","SWEPT_BODY",BODY,{"disambiguationData":[OSD([sQuery(id+"F32.wireOp",EDGE,"E112.bottom"),sQuery(id+"F32.wireOp",EDGE,"E112.top"),sQuery(id+"F32.wireOp",EDGE,"E112.left"),sQuery(id+"F32.wireOp",EDGE,"E112.right")])]}),"instanceName":"1"}),"instanceName":"1"});
            var Q1;
            Q1=makeQuery(id+"F38.opPattern","COPY",BODY,{"derivedFrom":makeQuery(id+"F36.opPattern","COPY",BODY,{"derivedFrom":makeQuery(id+"F34.opRevolve","SWEPT_BODY",BODY,{"disambiguationData":[OSD([sQuery(id+"F32.wireOp",EDGE,"E115.MirrorCS"),sQuery(id+"F32.wireOp",EDGE,"E116.MirrorCS"),sQuery(id+"F32.wireOp",EDGE,"E117.MirrorCS"),sQuery(id+"F32.wireOp",EDGE,"E118.MirrorCS")])]}),"instanceName":"1"}),"instanceName":"1"});
            var Q2;
            Q2=makeQuery(id+"F38.opPattern","COPY",BODY,{"derivedFrom":makeQuery(id+"F36.opPattern","COPY",BODY,{"derivedFrom":makeQuery(id+"F31.opRevolve","SWEPT_BODY",BODY,{"disambiguationData":[OSD([sQuery(id+"F29.wireOp",EDGE,"E104.MirrorCS"),sQuery(id+"F29.wireOp",EDGE,"E105.MirrorCS"),sQuery(id+"F29.wireOp",EDGE,"E106.MirrorCS"),sQuery(id+"F29.wireOp",EDGE,"E107.MirrorCS"),sQuery(id+"F29.wireOp",EDGE,"E108.MirrorCS"),sQuery(id+"F29.wireOp",EDGE,"E109.MirrorCS"),sQuery(id+"F29.wireOp",EDGE,"E110.MirrorCS")])]}),"instanceName":"1"}),"instanceName":"1"});
            var Q3;
            Q3=makeQuery(id+"F38.opPattern","COPY",BODY,{"derivedFrom":makeQuery(id+"F36.opPattern","COPY",BODY,{"derivedFrom":makeQuery(id+"F30.opRevolve","SWEPT_BODY",BODY,{"disambiguationData":[OSD([sQuery(id+"F29.wireOp",EDGE,"E98.0"),sQuery(id+"F29.wireOp",EDGE,"E99.top"),sQuery(id+"F29.wireOp",EDGE,"E100.left"),sQuery(id+"F29.wireOp",EDGE,"E105.MirrorCS")])]}),"instanceName":"1"}),"instanceName":"1"});
            var Q4;
            Q4=makeQuery(id+"F38.opPattern","COPY",BODY,{"derivedFrom":makeQuery(id+"F36.opPattern","COPY",BODY,{"derivedFrom":makeQuery(id+"F31.opRevolve","SWEPT_BODY",BODY,{"disambiguationData":[OSD([sQuery(id+"F29.wireOp",EDGE,"E100.bottom"),sQuery(id+"F29.wireOp",EDGE,"E100.top"),sQuery(id+"F29.wireOp",EDGE,"E100.left"),sQuery(id+"F29.wireOp",EDGE,"E100.right"),sQuery(id+"F29.wireOp",EDGE,"E101.bottom"),sQuery(id+"F29.wireOp",EDGE,"E101.top"),sQuery(id+"F29.wireOp",EDGE,"E101.left")])]}),"instanceName":"1"}),"instanceName":"1"});
            var Q5;
            Q5=sQuery(id+"F35.wireOp",EDGE,"E124");
            transform(context, id + "F39", {"entities" : qUnion([Q0, Q1, Q2, Q3, Q4]), "transformType" : TransformType.TRANSLATION_ENTITY, "oppositeDirectionEntity" : true, "transformLine" : qUnion([Q5]), "makeCopy" : false});
        }
        {
            var Q0;
            Q0=makeQuery(id+"F38.opPattern","COPY",BODY,{"derivedFrom":makeQuery(id+"F36.opPattern","COPY",BODY,{"derivedFrom":makeQuery(id+"F33.opRevolve","SWEPT_BODY",BODY,{"disambiguationData":[OSD([sQuery(id+"F32.wireOp",EDGE,"E112.bottom"),sQuery(id+"F32.wireOp",EDGE,"E112.top"),sQuery(id+"F32.wireOp",EDGE,"E112.left"),sQuery(id+"F32.wireOp",EDGE,"E112.right")])]}),"instanceName":"1"}),"instanceName":"1"});
            var Q1;
            Q1=makeQuery(id+"F38.opPattern","COPY",BODY,{"derivedFrom":makeQuery(id+"F36.opPattern","COPY",BODY,{"derivedFrom":makeQuery(id+"F34.opRevolve","SWEPT_BODY",BODY,{"disambiguationData":[OSD([sQuery(id+"F32.wireOp",EDGE,"E115.MirrorCS"),sQuery(id+"F32.wireOp",EDGE,"E116.MirrorCS"),sQuery(id+"F32.wireOp",EDGE,"E117.MirrorCS"),sQuery(id+"F32.wireOp",EDGE,"E118.MirrorCS")])]}),"instanceName":"1"}),"instanceName":"1"});
            var Q2;
            Q2=makeQuery(id+"F38.opPattern","COPY",BODY,{"derivedFrom":makeQuery(id+"F36.opPattern","COPY",BODY,{"derivedFrom":makeQuery(id+"F31.opRevolve","SWEPT_BODY",BODY,{"disambiguationData":[OSD([sQuery(id+"F29.wireOp",EDGE,"E104.MirrorCS"),sQuery(id+"F29.wireOp",EDGE,"E105.MirrorCS"),sQuery(id+"F29.wireOp",EDGE,"E106.MirrorCS"),sQuery(id+"F29.wireOp",EDGE,"E107.MirrorCS"),sQuery(id+"F29.wireOp",EDGE,"E108.MirrorCS"),sQuery(id+"F29.wireOp",EDGE,"E109.MirrorCS"),sQuery(id+"F29.wireOp",EDGE,"E110.MirrorCS")])]}),"instanceName":"1"}),"instanceName":"1"});
            var Q3;
            Q3=makeQuery(id+"F38.opPattern","COPY",BODY,{"derivedFrom":makeQuery(id+"F36.opPattern","COPY",BODY,{"derivedFrom":makeQuery(id+"F30.opRevolve","SWEPT_BODY",BODY,{"disambiguationData":[OSD([sQuery(id+"F29.wireOp",EDGE,"E98.0"),sQuery(id+"F29.wireOp",EDGE,"E99.top"),sQuery(id+"F29.wireOp",EDGE,"E100.left"),sQuery(id+"F29.wireOp",EDGE,"E105.MirrorCS")])]}),"instanceName":"1"}),"instanceName":"1"});
            var Q4;
            Q4=makeQuery(id+"F38.opPattern","COPY",BODY,{"derivedFrom":makeQuery(id+"F36.opPattern","COPY",BODY,{"derivedFrom":makeQuery(id+"F31.opRevolve","SWEPT_BODY",BODY,{"disambiguationData":[OSD([sQuery(id+"F29.wireOp",EDGE,"E100.bottom"),sQuery(id+"F29.wireOp",EDGE,"E100.top"),sQuery(id+"F29.wireOp",EDGE,"E100.left"),sQuery(id+"F29.wireOp",EDGE,"E100.right"),sQuery(id+"F29.wireOp",EDGE,"E101.bottom"),sQuery(id+"F29.wireOp",EDGE,"E101.top"),sQuery(id+"F29.wireOp",EDGE,"E101.left")])]}),"instanceName":"1"}),"instanceName":"1"});
            var Q5;
            Q5=sQuery(id+"F35.wireOp",EDGE,"E122");
            transform(context, id + "F40", {"entities" : qUnion([Q0, Q1, Q2, Q3, Q4]), "transformType" : TransformType.TRANSLATION_ENTITY, "oppositeDirectionEntity" : false, "transformLine" : qUnion([Q5]), "makeCopy" : true});
        }
        {
            var Q0;
            Q0=makeQuery(id+"F40.opPattern","COPY",BODY,{"derivedFrom":makeQuery(id+"F38.opPattern","COPY",BODY,{"derivedFrom":makeQuery(id+"F36.opPattern","COPY",BODY,{"derivedFrom":makeQuery(id+"F34.opRevolve","SWEPT_BODY",BODY,{"disambiguationData":[OSD([sQuery(id+"F32.wireOp",EDGE,"E115.MirrorCS"),sQuery(id+"F32.wireOp",EDGE,"E116.MirrorCS"),sQuery(id+"F32.wireOp",EDGE,"E117.MirrorCS"),sQuery(id+"F32.wireOp",EDGE,"E118.MirrorCS")])]}),"instanceName":"1"}),"instanceName":"1"}),"instanceName":"1"});
            var Q1;
            Q1=makeQuery(id+"F40.opPattern","COPY",BODY,{"derivedFrom":makeQuery(id+"F38.opPattern","COPY",BODY,{"derivedFrom":makeQuery(id+"F36.opPattern","COPY",BODY,{"derivedFrom":makeQuery(id+"F30.opRevolve","SWEPT_BODY",BODY,{"disambiguationData":[OSD([sQuery(id+"F29.wireOp",EDGE,"E98.0"),sQuery(id+"F29.wireOp",EDGE,"E99.top"),sQuery(id+"F29.wireOp",EDGE,"E100.left"),sQuery(id+"F29.wireOp",EDGE,"E105.MirrorCS")])]}),"instanceName":"1"}),"instanceName":"1"}),"instanceName":"1"});
            var Q2;
            Q2=makeQuery(id+"F40.opPattern","COPY",BODY,{"derivedFrom":makeQuery(id+"F38.opPattern","COPY",BODY,{"derivedFrom":makeQuery(id+"F36.opPattern","COPY",BODY,{"derivedFrom":makeQuery(id+"F31.opRevolve","SWEPT_BODY",BODY,{"disambiguationData":[OSD([sQuery(id+"F29.wireOp",EDGE,"E100.bottom"),sQuery(id+"F29.wireOp",EDGE,"E100.top"),sQuery(id+"F29.wireOp",EDGE,"E100.left"),sQuery(id+"F29.wireOp",EDGE,"E100.right"),sQuery(id+"F29.wireOp",EDGE,"E101.bottom"),sQuery(id+"F29.wireOp",EDGE,"E101.top"),sQuery(id+"F29.wireOp",EDGE,"E101.left")])]}),"instanceName":"1"}),"instanceName":"1"}),"instanceName":"1"});
            var Q3;
            Q3=makeQuery(id+"F40.opPattern","COPY",BODY,{"derivedFrom":makeQuery(id+"F38.opPattern","COPY",BODY,{"derivedFrom":makeQuery(id+"F36.opPattern","COPY",BODY,{"derivedFrom":makeQuery(id+"F31.opRevolve","SWEPT_BODY",BODY,{"disambiguationData":[OSD([sQuery(id+"F29.wireOp",EDGE,"E104.MirrorCS"),sQuery(id+"F29.wireOp",EDGE,"E105.MirrorCS"),sQuery(id+"F29.wireOp",EDGE,"E106.MirrorCS"),sQuery(id+"F29.wireOp",EDGE,"E107.MirrorCS"),sQuery(id+"F29.wireOp",EDGE,"E108.MirrorCS"),sQuery(id+"F29.wireOp",EDGE,"E109.MirrorCS"),sQuery(id+"F29.wireOp",EDGE,"E110.MirrorCS")])]}),"instanceName":"1"}),"instanceName":"1"}),"instanceName":"1"});
            var Q4;
            Q4=makeQuery(id+"F40.opPattern","COPY",BODY,{"derivedFrom":makeQuery(id+"F38.opPattern","COPY",BODY,{"derivedFrom":makeQuery(id+"F36.opPattern","COPY",BODY,{"derivedFrom":makeQuery(id+"F33.opRevolve","SWEPT_BODY",BODY,{"disambiguationData":[OSD([sQuery(id+"F32.wireOp",EDGE,"E112.bottom"),sQuery(id+"F32.wireOp",EDGE,"E112.top"),sQuery(id+"F32.wireOp",EDGE,"E112.left"),sQuery(id+"F32.wireOp",EDGE,"E112.right")])]}),"instanceName":"1"}),"instanceName":"1"}),"instanceName":"1"});
            var Q5;
            Q5=sQuery(id+"F35.wireOp",EDGE,"E125");
            transform(context, id + "F41", {"entities" : qUnion([Q0, Q1, Q2, Q3, Q4]), "transformType" : TransformType.TRANSLATION_ENTITY, "oppositeDirectionEntity" : true, "transformLine" : qUnion([Q5]), "makeCopy" : false});
        }
        {
            var Q0;
            Q0=qCreatedBy(makeId("Front.planeOp"),FACE);
            var sketch = newSketch(context, id + "F42", { "sketchPlane" : qUnion([Q0])});
            skLineSegment(sketch, "E126.0", {"start": v(1071.56, -457.93) * mm, "end": v(1087.44, -457.93) * mm, "construction": true});
            skLineSegment(sketch, "E126.1", {"start": v(1071.56, -508.73) * mm, "end": v(1087.44, -508.73) * mm, "construction": true});
            skLineSegment(sketch, "E126.2", {"start": v(1643.06, -457.93) * mm, "end": v(1658.94, -457.93) * mm, "construction": true});
            skLineSegment(sketch, "E126.3", {"start": v(1643.06, -508.73) * mm, "end": v(1658.94, -508.73) * mm, "construction": true});
            skLineSegment(sketch, "E127.0", {"start": v(1643.06, -19.78) * mm, "end": v(1658.94, -19.78) * mm, "construction": true});
            skLineSegment(sketch, "E127.1", {"start": v(1643.06, -70.58) * mm, "end": v(1658.94, -70.58) * mm, "construction": true});
            skLineSegment(sketch, "E128.0", {"start": v(1897.06, -19.78) * mm, "end": v(1912.94, -19.78) * mm, "construction": true});
            skLineSegment(sketch, "E128.1", {"start": v(1897.06, -70.58) * mm, "end": v(1912.94, -70.58) * mm, "construction": true});
            skLineSegment(sketch, "E129.0", {"start": v(1879.6, -694.52) * mm, "end": v(1930.4, -694.52) * mm, "construction": true});
            skLineSegment(sketch, "E130.0", {"start": v(1071.56, 221.52) * mm, "end": v(1087.44, 221.52) * mm, "construction": true});
            skLineSegment(sketch, "E130.1", {"start": v(1071.56, 272.32) * mm, "end": v(1087.44, 272.32) * mm, "construction": true});
            skLineSegment(sketch, "E130.2", {"start": v(817.56, 272.32) * mm, "end": v(833.44, 272.32) * mm, "construction": true});
            skLineSegment(sketch, "E130.3", {"start": v(817.56, 221.52) * mm, "end": v(833.44, 221.52) * mm, "construction": true});
            skLineSegment(sketch, "E131.0", {"start": v(817.56, -19.78) * mm, "end": v(833.44, -19.78) * mm, "construction": true});
            skLineSegment(sketch, "E131.1", {"start": v(817.56, -70.58) * mm, "end": v(833.44, -70.58) * mm, "construction": true});
            skLineSegment(sketch, "E132.0", {"start": v(246.06, -19.78) * mm, "end": v(261.94, -19.78) * mm, "construction": true});
            skLineSegment(sketch, "E132.1", {"start": v(246.06, -70.58) * mm, "end": v(261.94, -70.58) * mm, "construction": true});
            skLineSegment(sketch, "E133.0", {"start": v(246.06, -305.53) * mm, "end": v(261.94, -305.53) * mm, "construction": true});
            skLineSegment(sketch, "E133.1", {"start": v(246.06, -356.33) * mm, "end": v(261.94, -356.33) * mm, "construction": true});
            skLineSegment(sketch, "E134.0", {"start": v(-7.94, -305.53) * mm, "end": v(7.94, -305.53) * mm, "construction": true});
            skLineSegment(sketch, "E134.1", {"start": v(-7.94, -356.33) * mm, "end": v(7.94, -356.33) * mm, "construction": true});
            skLineSegment(sketch, "E135.0", {"start": v(-7.94, 431.07) * mm, "end": v(7.94, 431.07) * mm, "construction": true});
            skLineSegment(sketch, "E135.1", {"start": v(-7.94, 380.27) * mm, "end": v(7.94, 380.27) * mm, "construction": true});
            skLineSegment(sketch, "E136.0", {"start": v(-261.94, 431.07) * mm, "end": v(-246.06, 431.07) * mm, "construction": true});
            skLineSegment(sketch, "E136.1", {"start": v(-261.94, 380.27) * mm, "end": v(-246.06, 380.27) * mm, "construction": true});
            skLineSegment(sketch, "E137.0", {"start": v(-261.94, -508.73) * mm, "end": v(-246.06, -508.73) * mm, "construction": true});
            skLineSegment(sketch, "E137.1", {"start": v(-261.94, -457.93) * mm, "end": v(-246.06, -457.93) * mm, "construction": true});
            skLineSegment(sketch, "E138.0", {"start": v(-833.44, -457.93) * mm, "end": v(-817.56, -457.93) * mm, "construction": true});
            skLineSegment(sketch, "E138.1", {"start": v(-833.44, -508.73) * mm, "end": v(-817.56, -508.73) * mm, "construction": true});
            skLineSegment(sketch, "E139.0", {"start": v(-833.44, -19.78) * mm, "end": v(-817.56, -19.78) * mm, "construction": true});
            skLineSegment(sketch, "E140.0", {"start": v(-1087.44, -19.78) * mm, "end": v(-1071.56, -19.78) * mm, "construction": true});
            skLineSegment(sketch, "E140.1", {"start": v(-1087.44, -70.58) * mm, "end": v(-1071.56, -70.58) * mm, "construction": true});
            skLineSegment(sketch, "E141.0", {"start": v(-1087.44, 272.32) * mm, "end": v(-1071.56, 272.32) * mm, "construction": true});
            skLineSegment(sketch, "E141.1", {"start": v(-1087.44, 221.52) * mm, "end": v(-1071.56, 221.52) * mm, "construction": true});
            skLineSegment(sketch, "E142.0", {"start": v(-1658.94, 272.32) * mm, "end": v(-1643.06, 272.32) * mm, "construction": true});
            skLineSegment(sketch, "E142.1", {"start": v(-1658.94, 221.52) * mm, "end": v(-1643.06, 221.52) * mm, "construction": true});
            skLineSegment(sketch, "E143.0", {"start": v(-1658.94, -356.33) * mm, "end": v(-1643.06, -356.33) * mm, "construction": true});
            skLineSegment(sketch, "E143.1", {"start": v(-1658.94, -305.53) * mm, "end": v(-1643.06, -305.53) * mm, "construction": true});
            skLineSegment(sketch, "E144.0", {"start": v(-1912.94, -305.53) * mm, "end": v(-1897.06, -305.53) * mm, "construction": true});
            skLineSegment(sketch, "E144.1", {"start": v(-1912.94, -356.33) * mm, "end": v(-1897.06, -356.33) * mm, "construction": true});
            skLineSegment(sketch, "E145.0", {"start": v(-1930.4, -783.42) * mm, "end": v(-1879.6, -783.42) * mm, "construction": true});
            skLineSegment(sketch, "E146.0", {"start": v(228.6, -783.42) * mm, "end": v(279.4, -783.42) * mm, "construction": true});
            skLineSegment(sketch, "E147.0", {"start": v(-1905, 1053.37) * mm, "end": v(-1905, -788.13) * mm, "construction": true});
            skLineSegment(sketch, "E147.1", {"start": v(-1651, 1053.37) * mm, "end": v(-1651, -788.13) * mm, "construction": true});
            skLineSegment(sketch, "E147.2", {"start": v(-1079.5, 1053.37) * mm, "end": v(-1079.5, -788.13) * mm, "construction": true});
            skLineSegment(sketch, "E147.3", {"start": v(-825.5, 1053.37) * mm, "end": v(-825.5, -788.13) * mm, "construction": true});
            skLineSegment(sketch, "E147.4", {"start": v(-254, 1053.37) * mm, "end": v(-254, -788.13) * mm, "construction": true});
            skLineSegment(sketch, "E147.5", {"start": v(0, 1053.37) * mm, "end": v(0, -788.13) * mm, "construction": true});
            skLineSegment(sketch, "E147.6", {"start": v(254, 1053.37) * mm, "end": v(254, -788.13) * mm, "construction": true});
            skLineSegment(sketch, "E147.7", {"start": v(825.5, 1053.37) * mm, "end": v(825.5, -788.13) * mm, "construction": true});
            skLineSegment(sketch, "E147.8", {"start": v(1079.5, 1053.37) * mm, "end": v(1079.5, -788.13) * mm, "construction": true});
            skLineSegment(sketch, "E147.9", {"start": v(1651, 1053.37) * mm, "end": v(1651, -788.13) * mm, "construction": true});
            skLineSegment(sketch, "E147.10", {"start": v(1905, 1053.37) * mm, "end": v(1905, -788.13) * mm, "construction": true});
            skLineSegment(sketch, "E147.11", {"start": v(1955.8, 1053.37) * mm, "end": v(1955.8, -788.13) * mm, "construction": true});
            skLineSegment(sketch, "E148.bottom", {"start": v(-1912.94, -356.33) * mm, "end": v(-1905, -356.33) * mm});
            skLineSegment(sketch, "E148.top", {"start": v(-1912.94, -783.42) * mm, "end": v(-1905, -783.42) * mm});
            skLineSegment(sketch, "E148.left", {"start": v(-1912.94, -356.33) * mm, "end": v(-1912.94, -783.42) * mm});
            skLineSegment(sketch, "E148.right", {"start": v(-1905, -356.33) * mm, "end": v(-1905, -783.42) * mm});
            skLineSegment(sketch, "E149.bottom", {"start": v(-1912.94, -305.53) * mm, "end": v(-1905, -305.53) * mm});
            skLineSegment(sketch, "E149.top", {"start": v(-1912.94, 1053.37) * mm, "end": v(-1905, 1053.37) * mm});
            skLineSegment(sketch, "E149.left", {"start": v(-1912.94, -305.53) * mm, "end": v(-1912.94, 1053.37) * mm});
            skLineSegment(sketch, "E149.right", {"start": v(-1905, -305.53) * mm, "end": v(-1905, 1053.37) * mm});
            skLineSegment(sketch, "E150.bottom", {"start": v(-1658.94, 272.32) * mm, "end": v(-1651, 272.32) * mm});
            skLineSegment(sketch, "E150.top", {"start": v(-1658.94, 1053.37) * mm, "end": v(-1651, 1053.37) * mm});
            skLineSegment(sketch, "E150.left", {"start": v(-1658.94, 272.32) * mm, "end": v(-1658.94, 1053.37) * mm});
            skLineSegment(sketch, "E150.right", {"start": v(-1651, 272.32) * mm, "end": v(-1651, 1053.37) * mm});
            skLineSegment(sketch, "E151.bottom", {"start": v(-1658.94, 221.52) * mm, "end": v(-1651, 221.52) * mm});
            skLineSegment(sketch, "E151.top", {"start": v(-1658.94, -305.53) * mm, "end": v(-1651, -305.53) * mm});
            skLineSegment(sketch, "E151.left", {"start": v(-1658.94, 221.52) * mm, "end": v(-1658.94, -305.53) * mm});
            skLineSegment(sketch, "E151.right", {"start": v(-1651, 221.52) * mm, "end": v(-1651, -305.53) * mm});
            skLineSegment(sketch, "E152.bottom", {"start": v(-1087.44, 272.32) * mm, "end": v(-1079.5, 272.32) * mm});
            skLineSegment(sketch, "E152.top", {"start": v(-1087.44, 1053.37) * mm, "end": v(-1079.5, 1053.37) * mm});
            skLineSegment(sketch, "E152.left", {"start": v(-1087.44, 272.32) * mm, "end": v(-1087.44, 1053.37) * mm});
            skLineSegment(sketch, "E152.right", {"start": v(-1079.5, 272.32) * mm, "end": v(-1079.5, 1053.37) * mm});
            skLineSegment(sketch, "E153.bottom", {"start": v(-1087.44, 221.52) * mm, "end": v(-1079.5, 221.52) * mm});
            skLineSegment(sketch, "E153.top", {"start": v(-1087.44, -19.78) * mm, "end": v(-1079.5, -19.78) * mm});
            skLineSegment(sketch, "E153.left", {"start": v(-1087.44, 221.52) * mm, "end": v(-1087.44, -19.78) * mm});
            skLineSegment(sketch, "E153.right", {"start": v(-1079.5, 221.52) * mm, "end": v(-1079.5, -19.78) * mm});
            skLineSegment(sketch, "E154.bottom", {"start": v(-1087.44, -70.58) * mm, "end": v(-1079.5, -70.58) * mm});
            skLineSegment(sketch, "E154.top", {"start": v(-1087.44, -775.43) * mm, "end": v(-1079.5, -775.43) * mm});
            skLineSegment(sketch, "E154.left", {"start": v(-1087.44, -70.58) * mm, "end": v(-1087.44, -775.43) * mm});
            skLineSegment(sketch, "E154.right", {"start": v(-1079.5, -70.58) * mm, "end": v(-1079.5, -775.43) * mm});
            skLineSegment(sketch, "E155.0", {"start": v(-1087.44, -775.43) * mm, "end": v(-1071.56, -775.43) * mm, "construction": true});
            skLineSegment(sketch, "E155.1", {"start": v(-833.44, -775.43) * mm, "end": v(-817.56, -775.43) * mm, "construction": true});
            skLineSegment(sketch, "E156.bottom", {"start": v(-833.44, -775.43) * mm, "end": v(-825.5, -775.43) * mm});
            skLineSegment(sketch, "E156.top", {"start": v(-833.44, -508.73) * mm, "end": v(-825.5, -508.73) * mm});
            skLineSegment(sketch, "E156.left", {"start": v(-833.44, -775.43) * mm, "end": v(-833.44, -508.73) * mm});
            skLineSegment(sketch, "E156.right", {"start": v(-825.5, -775.43) * mm, "end": v(-825.5, -508.73) * mm});
            skLineSegment(sketch, "E157.bottom", {"start": v(-833.44, -457.93) * mm, "end": v(-825.5, -457.93) * mm});
            skLineSegment(sketch, "E157.top", {"start": v(-833.44, -70.58) * mm, "end": v(-825.5, -70.58) * mm});
            skLineSegment(sketch, "E157.left", {"start": v(-833.44, -457.93) * mm, "end": v(-833.44, -70.58) * mm});
            skLineSegment(sketch, "E157.right", {"start": v(-825.5, -457.93) * mm, "end": v(-825.5, -70.58) * mm});
            skLineSegment(sketch, "E158.0", {"start": v(-833.44, -70.58) * mm, "end": v(-817.56, -70.58) * mm, "construction": true});
            skLineSegment(sketch, "E159.bottom", {"start": v(-833.44, -19.78) * mm, "end": v(-825.5, -19.78) * mm});
            skLineSegment(sketch, "E159.top", {"start": v(-833.44, 1053.37) * mm, "end": v(-825.5, 1053.37) * mm});
            skLineSegment(sketch, "E159.left", {"start": v(-833.44, -19.78) * mm, "end": v(-833.44, 1053.37) * mm});
            skLineSegment(sketch, "E159.right", {"start": v(-825.5, -19.78) * mm, "end": v(-825.5, 1053.37) * mm});
            skLineSegment(sketch, "E160.bottom", {"start": v(-261.94, 431.07) * mm, "end": v(-254, 431.07) * mm});
            skLineSegment(sketch, "E160.top", {"start": v(-261.94, 1053.37) * mm, "end": v(-254, 1053.37) * mm});
            skLineSegment(sketch, "E160.left", {"start": v(-261.94, 431.07) * mm, "end": v(-261.94, 1053.37) * mm});
            skLineSegment(sketch, "E160.right", {"start": v(-254, 431.07) * mm, "end": v(-254, 1053.37) * mm});
            skLineSegment(sketch, "E161.bottom", {"start": v(-261.94, 380.27) * mm, "end": v(-254, 380.27) * mm});
            skLineSegment(sketch, "E161.top", {"start": v(-261.94, -457.93) * mm, "end": v(-254, -457.93) * mm});
            skLineSegment(sketch, "E161.left", {"start": v(-261.94, 380.27) * mm, "end": v(-261.94, -457.93) * mm});
            skLineSegment(sketch, "E161.right", {"start": v(-254, 380.27) * mm, "end": v(-254, -457.93) * mm});
            skLineSegment(sketch, "E162.bottom", {"start": v(-7.94, 431.07) * mm, "end": v(0, 431.07) * mm});
            skLineSegment(sketch, "E162.top", {"start": v(-7.94, 1053.37) * mm, "end": v(0, 1053.37) * mm});
            skLineSegment(sketch, "E162.left", {"start": v(-7.94, 431.07) * mm, "end": v(-7.94, 1053.37) * mm});
            skLineSegment(sketch, "E162.right", {"start": v(0, 431.07) * mm, "end": v(0, 1053.37) * mm});
            skLineSegment(sketch, "E163.bottom", {"start": v(-7.94, 380.27) * mm, "end": v(0, 380.27) * mm});
            skLineSegment(sketch, "E163.top", {"start": v(-7.94, -305.53) * mm, "end": v(0, -305.53) * mm});
            skLineSegment(sketch, "E163.left", {"start": v(-7.94, 380.27) * mm, "end": v(-7.94, -305.53) * mm});
            skLineSegment(sketch, "E163.right", {"start": v(0, 380.27) * mm, "end": v(0, -305.53) * mm});
            skLineSegment(sketch, "E164.bottom", {"start": v(246.06, -305.53) * mm, "end": v(254, -305.53) * mm});
            skLineSegment(sketch, "E164.top", {"start": v(246.06, -70.58) * mm, "end": v(254, -70.58) * mm});
            skLineSegment(sketch, "E164.left", {"start": v(246.06, -305.53) * mm, "end": v(246.06, -70.58) * mm});
            skLineSegment(sketch, "E164.right", {"start": v(254, -305.53) * mm, "end": v(254, -70.58) * mm});
            skLineSegment(sketch, "E165.bottom", {"start": v(246.06, -19.78) * mm, "end": v(254, -19.78) * mm});
            skLineSegment(sketch, "E165.top", {"start": v(246.06, 1053.37) * mm, "end": v(254, 1053.37) * mm});
            skLineSegment(sketch, "E165.left", {"start": v(246.06, -19.78) * mm, "end": v(246.06, 1053.37) * mm});
            skLineSegment(sketch, "E165.right", {"start": v(254, -19.78) * mm, "end": v(254, 1053.37) * mm});
            skLineSegment(sketch, "E166.bottom", {"start": v(817.56, -19.78) * mm, "end": v(825.5, -19.78) * mm});
            skLineSegment(sketch, "E166.top", {"start": v(817.56, 221.52) * mm, "end": v(825.5, 221.52) * mm});
            skLineSegment(sketch, "E166.left", {"start": v(817.56, -19.78) * mm, "end": v(817.56, 221.52) * mm});
            skLineSegment(sketch, "E166.right", {"start": v(825.5, -19.78) * mm, "end": v(825.5, 221.52) * mm});
            skLineSegment(sketch, "E167.bottom", {"start": v(825.5, 1053.37) * mm, "end": v(817.56, 1053.37) * mm});
            skLineSegment(sketch, "E167.top", {"start": v(825.5, 272.32) * mm, "end": v(817.56, 272.32) * mm});
            skLineSegment(sketch, "E167.left", {"start": v(825.5, 1053.37) * mm, "end": v(825.5, 272.32) * mm});
            skLineSegment(sketch, "E167.right", {"start": v(817.56, 1053.37) * mm, "end": v(817.56, 272.32) * mm});
            skLineSegment(sketch, "E168.bottom", {"start": v(1071.56, 272.32) * mm, "end": v(1079.5, 272.32) * mm});
            skLineSegment(sketch, "E168.top", {"start": v(1071.56, 1053.37) * mm, "end": v(1079.5, 1053.37) * mm});
            skLineSegment(sketch, "E168.left", {"start": v(1071.56, 272.32) * mm, "end": v(1071.56, 1053.37) * mm});
            skLineSegment(sketch, "E168.right", {"start": v(1079.5, 272.32) * mm, "end": v(1079.5, 1053.37) * mm});
            skLineSegment(sketch, "E169.bottom", {"start": v(1071.56, 221.52) * mm, "end": v(1079.5, 221.52) * mm});
            skLineSegment(sketch, "E169.top", {"start": v(1071.56, -457.93) * mm, "end": v(1079.5, -457.93) * mm});
            skLineSegment(sketch, "E169.left", {"start": v(1071.56, 221.52) * mm, "end": v(1071.56, -457.93) * mm});
            skLineSegment(sketch, "E169.right", {"start": v(1079.5, 221.52) * mm, "end": v(1079.5, -457.93) * mm});
            skLineSegment(sketch, "E170.bottom", {"start": v(1643.06, -457.93) * mm, "end": v(1651, -457.93) * mm});
            skLineSegment(sketch, "E170.top", {"start": v(1643.06, -70.58) * mm, "end": v(1651, -70.58) * mm});
            skLineSegment(sketch, "E170.left", {"start": v(1643.06, -457.93) * mm, "end": v(1643.06, -70.58) * mm});
            skLineSegment(sketch, "E170.right", {"start": v(1651, -457.93) * mm, "end": v(1651, -70.58) * mm});
            skLineSegment(sketch, "E171.bottom", {"start": v(1643.06, -19.78) * mm, "end": v(1651, -19.78) * mm});
            skLineSegment(sketch, "E171.top", {"start": v(1643.06, 1053.37) * mm, "end": v(1651, 1053.37) * mm});
            skLineSegment(sketch, "E171.left", {"start": v(1643.06, -19.78) * mm, "end": v(1643.06, 1053.37) * mm});
            skLineSegment(sketch, "E171.right", {"start": v(1651, -19.78) * mm, "end": v(1651, 1053.37) * mm});
            skLineSegment(sketch, "E172.bottom", {"start": v(1897.06, -19.78) * mm, "end": v(1905, -19.78) * mm});
            skLineSegment(sketch, "E172.top", {"start": v(1897.06, 1053.37) * mm, "end": v(1905, 1053.37) * mm});
            skLineSegment(sketch, "E172.left", {"start": v(1897.06, -19.78) * mm, "end": v(1897.06, 1053.37) * mm});
            skLineSegment(sketch, "E172.right", {"start": v(1905, -19.78) * mm, "end": v(1905, 1053.37) * mm});
            skLineSegment(sketch, "E173.bottom", {"start": v(1897.06, -70.58) * mm, "end": v(1905, -70.58) * mm});
            skLineSegment(sketch, "E173.top", {"start": v(1897.06, -694.52) * mm, "end": v(1905, -694.52) * mm});
            skLineSegment(sketch, "E173.left", {"start": v(1897.06, -70.58) * mm, "end": v(1897.06, -694.52) * mm});
            skLineSegment(sketch, "E173.right", {"start": v(1905, -70.58) * mm, "end": v(1905, -694.52) * mm});
            skLineSegment(sketch, "E174.bottom", {"start": v(246.06, -356.33) * mm, "end": v(254, -356.33) * mm});
            skLineSegment(sketch, "E174.top", {"start": v(246.06, -783.42) * mm, "end": v(254, -783.42) * mm});
            skLineSegment(sketch, "E174.left", {"start": v(246.06, -356.33) * mm, "end": v(246.06, -783.42) * mm});
            skLineSegment(sketch, "E174.right", {"start": v(254, -356.33) * mm, "end": v(254, -783.42) * mm});
            skSolve(sketch);
        }
        {
            var Q0;
            Q0=makeQuery(id+"F42.imprint","IMPRINT",FACE,{"disambiguationData":[TD([[makeQuery(id+"F42.imprint","IMPRINT",EDGE,{"derivedFrom":sQuery(id+"F42.wireOp",EDGE,"E149.bottom")}),1.0]])]});
            var Q1;
            Q1=makeQuery(id+"F42.imprint","IMPRINT",FACE,{"disambiguationData":[TD([[makeQuery(id+"F42.imprint","IMPRINT",EDGE,{"derivedFrom":sQuery(id+"F42.wireOp",EDGE,"E148.bottom")}),-1.0]])]});
            var Q2;
            Q2=sQuery(id+"F42.wireOp",EDGE,"E148.right");
            revolve(context, id + "F43", {"entities" : qUnion([Q0, Q1]), "axis" : qUnion([Q2]), "revolveType" : RevolveType.FULL});
        }
        {
            var Q0;
            Q0=makeQuery(id+"F42.imprint","IMPRINT",FACE,{"disambiguationData":[TD([[makeQuery(id+"F42.imprint","IMPRINT",EDGE,{"derivedFrom":sQuery(id+"F42.wireOp",EDGE,"E151.bottom")}),-1.0]])]});
            var Q1;
            Q1=makeQuery(id+"F42.imprint","IMPRINT",FACE,{"disambiguationData":[TD([[makeQuery(id+"F42.imprint","IMPRINT",EDGE,{"derivedFrom":sQuery(id+"F42.wireOp",EDGE,"E150.bottom")}),1.0]])]});
            var Q2;
            Q2=sQuery(id+"F42.wireOp",EDGE,"E150.right");
            revolve(context, id + "F44", {"entities" : qUnion([Q0, Q1]), "axis" : qUnion([Q2]), "revolveType" : RevolveType.FULL});
        }
        {
            var Q0;
            Q0=makeQuery(id+"F42.imprint","IMPRINT",FACE,{"disambiguationData":[TD([[makeQuery(id+"F42.imprint","IMPRINT",EDGE,{"derivedFrom":sQuery(id+"F42.wireOp",EDGE,"E152.bottom")}),1.0]])]});
            var Q1;
            Q1=makeQuery(id+"F42.imprint","IMPRINT",FACE,{"disambiguationData":[TD([[makeQuery(id+"F42.imprint","IMPRINT",EDGE,{"derivedFrom":sQuery(id+"F42.wireOp",EDGE,"E153.bottom")}),-1.0]])]});
            var Q2;
            Q2=makeQuery(id+"F42.imprint","IMPRINT",FACE,{"disambiguationData":[TD([[makeQuery(id+"F42.imprint","IMPRINT",EDGE,{"derivedFrom":sQuery(id+"F42.wireOp",EDGE,"E154.bottom")}),-1.0]])]});
            var Q3;
            Q3=sQuery(id+"F42.wireOp",EDGE,"E154.right");
            revolve(context, id + "F45", {"entities" : qUnion([Q0, Q1, Q2]), "axis" : qUnion([Q3]), "revolveType" : RevolveType.FULL});
        }
        {
            var Q0;
            Q0=makeQuery(id+"F42.imprint","IMPRINT",FACE,{"disambiguationData":[TD([[makeQuery(id+"F42.imprint","IMPRINT",EDGE,{"derivedFrom":sQuery(id+"F42.wireOp",EDGE,"E159.bottom")}),1.0]])]});
            var Q1;
            Q1=makeQuery(id+"F42.imprint","IMPRINT",FACE,{"disambiguationData":[TD([[makeQuery(id+"F42.imprint","IMPRINT",EDGE,{"derivedFrom":sQuery(id+"F42.wireOp",EDGE,"E157.bottom")}),1.0]])]});
            var Q2;
            Q2=makeQuery(id+"F42.imprint","IMPRINT",FACE,{"disambiguationData":[TD([[makeQuery(id+"F42.imprint","IMPRINT",EDGE,{"derivedFrom":sQuery(id+"F42.wireOp",EDGE,"E156.bottom")}),1.0]])]});
            var Q3;
            Q3=sQuery(id+"F42.wireOp",EDGE,"E156.right");
            revolve(context, id + "F46", {"entities" : qUnion([Q0, Q1, Q2]), "axis" : qUnion([Q3]), "revolveType" : RevolveType.FULL});
        }
        {
            var Q0;
            Q0=makeQuery(id+"F42.imprint","IMPRINT",FACE,{"disambiguationData":[TD([[makeQuery(id+"F42.imprint","IMPRINT",EDGE,{"derivedFrom":sQuery(id+"F42.wireOp",EDGE,"E161.bottom")}),-1.0]])]});
            var Q1;
            Q1=makeQuery(id+"F42.imprint","IMPRINT",FACE,{"disambiguationData":[TD([[makeQuery(id+"F42.imprint","IMPRINT",EDGE,{"derivedFrom":sQuery(id+"F42.wireOp",EDGE,"E160.bottom")}),1.0]])]});
            var Q2;
            Q2=sQuery(id+"F42.wireOp",EDGE,"E160.right");
            revolve(context, id + "F47", {"entities" : qUnion([Q0, Q1]), "axis" : qUnion([Q2]), "revolveType" : RevolveType.FULL});
        }
        {
            var Q0;
            Q0=makeQuery(id+"F42.imprint","IMPRINT",FACE,{"disambiguationData":[TD([[makeQuery(id+"F42.imprint","IMPRINT",EDGE,{"derivedFrom":sQuery(id+"F42.wireOp",EDGE,"E163.bottom")}),-1.0]])]});
            var Q1;
            Q1=makeQuery(id+"F42.imprint","IMPRINT",FACE,{"disambiguationData":[TD([[makeQuery(id+"F42.imprint","IMPRINT",EDGE,{"derivedFrom":sQuery(id+"F42.wireOp",EDGE,"E162.bottom")}),1.0]])]});
            var Q2;
            Q2=sQuery(id+"F42.wireOp",EDGE,"E162.right");
            revolve(context, id + "F48", {"entities" : qUnion([Q0, Q1]), "axis" : qUnion([Q2]), "revolveType" : RevolveType.FULL});
        }
        {
            var Q0;
            Q0=makeQuery(id+"F42.imprint","IMPRINT",FACE,{"disambiguationData":[TD([[makeQuery(id+"F42.imprint","IMPRINT",EDGE,{"derivedFrom":sQuery(id+"F42.wireOp",EDGE,"E174.bottom")}),-1.0]])]});
            var Q1;
            Q1=makeQuery(id+"F42.imprint","IMPRINT",FACE,{"disambiguationData":[TD([[makeQuery(id+"F42.imprint","IMPRINT",EDGE,{"derivedFrom":sQuery(id+"F42.wireOp",EDGE,"E164.bottom")}),1.0]])]});
            var Q2;
            Q2=makeQuery(id+"F42.imprint","IMPRINT",FACE,{"disambiguationData":[TD([[makeQuery(id+"F42.imprint","IMPRINT",EDGE,{"derivedFrom":sQuery(id+"F42.wireOp",EDGE,"E165.bottom")}),1.0]])]});
            var Q3;
            Q3=sQuery(id+"F42.wireOp",EDGE,"E164.right");
            revolve(context, id + "F49", {"entities" : qUnion([Q0, Q1, Q2]), "axis" : qUnion([Q3]), "revolveType" : RevolveType.FULL});
        }
        {
            var Q0;
            Q0=makeQuery(id+"F42.imprint","IMPRINT",FACE,{"disambiguationData":[TD([[makeQuery(id+"F42.imprint","IMPRINT",EDGE,{"derivedFrom":sQuery(id+"F42.wireOp",EDGE,"E167.bottom")}),1.0]])]});
            var Q1;
            Q1=makeQuery(id+"F42.imprint","IMPRINT",FACE,{"disambiguationData":[TD([[makeQuery(id+"F42.imprint","IMPRINT",EDGE,{"derivedFrom":sQuery(id+"F42.wireOp",EDGE,"E166.bottom")}),1.0]])]});
            var Q2;
            Q2=sQuery(id+"F42.wireOp",EDGE,"E166.right");
            revolve(context, id + "F50", {"entities" : qUnion([Q0, Q1]), "axis" : qUnion([Q2]), "revolveType" : RevolveType.FULL});
        }
        {
            var Q0;
            Q0=makeQuery(id+"F42.imprint","IMPRINT",FACE,{"disambiguationData":[TD([[makeQuery(id+"F42.imprint","IMPRINT",EDGE,{"derivedFrom":sQuery(id+"F42.wireOp",EDGE,"E168.bottom")}),1.0]])]});
            var Q1;
            Q1=makeQuery(id+"F42.imprint","IMPRINT",FACE,{"disambiguationData":[TD([[makeQuery(id+"F42.imprint","IMPRINT",EDGE,{"derivedFrom":sQuery(id+"F42.wireOp",EDGE,"E169.bottom")}),-1.0]])]});
            var Q2;
            Q2=sQuery(id+"F42.wireOp",EDGE,"E169.right");
            revolve(context, id + "F51", {"entities" : qUnion([Q0, Q1]), "axis" : qUnion([Q2]), "revolveType" : RevolveType.FULL});
        }
        {
            var Q0;
            Q0=makeQuery(id+"F42.imprint","IMPRINT",FACE,{"disambiguationData":[TD([[makeQuery(id+"F42.imprint","IMPRINT",EDGE,{"derivedFrom":sQuery(id+"F42.wireOp",EDGE,"E170.bottom")}),1.0]])]});
            var Q1;
            Q1=makeQuery(id+"F42.imprint","IMPRINT",FACE,{"disambiguationData":[TD([[makeQuery(id+"F42.imprint","IMPRINT",EDGE,{"derivedFrom":sQuery(id+"F42.wireOp",EDGE,"E171.bottom")}),1.0]])]});
            var Q2;
            Q2=sQuery(id+"F42.wireOp",EDGE,"E170.right");
            revolve(context, id + "F52", {"entities" : qUnion([Q0, Q1]), "axis" : qUnion([Q2]), "revolveType" : RevolveType.FULL});
        }
        {
            var Q0;
            Q0=makeQuery(id+"F42.imprint","IMPRINT",FACE,{"disambiguationData":[TD([[makeQuery(id+"F42.imprint","IMPRINT",EDGE,{"derivedFrom":sQuery(id+"F42.wireOp",EDGE,"E172.bottom")}),1.0]])]});
            var Q1;
            Q1=makeQuery(id+"F42.imprint","IMPRINT",FACE,{"disambiguationData":[TD([[makeQuery(id+"F42.imprint","IMPRINT",EDGE,{"derivedFrom":sQuery(id+"F42.wireOp",EDGE,"E173.bottom")}),-1.0]])]});
            var Q2;
            Q2=sQuery(id+"F42.wireOp",EDGE,"E173.right");
            revolve(context, id + "F53", {"entities" : qUnion([Q0, Q1]), "axis" : qUnion([Q2]), "revolveType" : RevolveType.FULL});
        }
        {
            var Q0;
            Q0=makeQuery(id+"F2.opExtrude","SWEPT_FACE",FACE,{"disambiguationData":[OSD([sQuery(id+"F1.wireOp",EDGE,"E56.0.3")])]});
            var sketch = newSketch(context, id + "F54", { "sketchPlane" : qUnion([Q0])});
            skLineSegment(sketch, "E175.0", {"start": v(1955.8, 76.2) * mm, "end": v(-1955.8, 76.2) * mm, "construction": true});
            skLineSegment(sketch, "E176.0", {"start": v(1955.8, -76.2) * mm, "end": v(-1955.8, -76.2) * mm, "construction": true});
            skLineSegment(sketch, "E176.1", {"start": v(-1955.8, -76.2) * mm, "end": v(-1955.8, 76.2) * mm, "construction": true});
            skLineSegment(sketch, "E176.2", {"start": v(1955.8, -76.2) * mm, "end": v(1955.8, 76.2) * mm, "construction": true});
            skPoint(sketch, "E176.3", {"position": v(-1955.8, 0) * mm});
            skLineSegment(sketch, "E177.0", {"start": v(1953.77, 74.17) * mm, "end": v(-1953.77, 74.17) * mm});
            skLineSegment(sketch, "E177.1", {"start": v(1953.77, -74.17) * mm, "end": v(1953.77, 74.17) * mm});
            skLineSegment(sketch, "E177.2", {"start": v(1953.77, -74.17) * mm, "end": v(-1953.77, -74.17) * mm});
            skLineSegment(sketch, "E177.3", {"start": v(-1953.77, -74.17) * mm, "end": v(-1953.77, 74.17) * mm});
            skSolve(sketch);
        }
        {
            var Q0;
            Q0 = qSketchRegion(id + "F54", true);
            var Q1;
            Q1 = qConstructionFilter(qBodyType(qCreatedBy(id + "F54" ,EDGE), BodyType.WIRE), ConstructionObject.NO);
            extrude(context, id + "F55", {"entities" : qUnion([Q0]), "operationType" : NewBodyOperationType.REMOVE, "surfaceEntities" : qUnion([Q1]), "oppositeDirection" : true, "depth" : 36.07 * mm});
        }
        {
            var Q0;
            Q0=makeQuery(id+"F55.boolean.opBoolean","COPY",FACE,{"derivedFrom":makeQuery(id+"F55.opExtrude","SWEPT_FACE",FACE,{"disambiguationData":[OSD([sQuery(id+"F54.wireOp",EDGE,"E177.3")])]})});
            var sketch = newSketch(context, id + "F56", { "sketchPlane" : qUnion([Q0])});
            skLineSegment(sketch, "E178.0", {"start": v(0, 1091.47) * mm, "end": v(74.17, 1091.47) * mm});
            skLineSegment(sketch, "E178.1", {"start": v(74.17, 1055.4) * mm, "end": v(74.17, 1091.47) * mm, "construction": true});
            skLineSegment(sketch, "E179", {"start": v(74.17, 1091.47) * mm, "end": v(74.17, 1057) * mm});
            skLineSegment(sketch, "E180", {"start": v(74.17, 1057) * mm, "end": v(72.14, 1057) * mm});
            skLineSegment(sketch, "E181", {"start": v(72.14, 1057) * mm, "end": v(72.14, 1089.44) * mm});
            skLineSegment(sketch, "E182", {"start": v(72.14, 1089.44) * mm, "end": v(0, 1089.44) * mm});
            skLineSegment(sketch, "E183", {"start": v(0, 1089.44) * mm, "end": v(0, 1091.47) * mm, "construction": true});
            skPoint(sketch, "E184.orphan", {"position": v(-74.17, 1091.47) * mm});
            skLineSegment(sketch, "E185", {"start": v(0, 1091.47) * mm, "end": v(0, 1099.28) * mm, "construction": true});
            skLineSegment(sketch, "E186.MirrorCS", {"start": v(-72.14, 1089.44) * mm, "end": v(0, 1089.44) * mm});
            skLineSegment(sketch, "E187.MirrorCS", {"start": v(0, 1091.47) * mm, "end": v(-74.17, 1091.47) * mm});
            skLineSegment(sketch, "E188.MirrorCS", {"start": v(-74.17, 1055.4) * mm, "end": v(-74.17, 1091.47) * mm, "construction": true});
            skLineSegment(sketch, "E189.MirrorCS", {"start": v(-72.14, 1057) * mm, "end": v(-72.14, 1089.44) * mm});
            skLineSegment(sketch, "E190.MirrorCS", {"start": v(-74.17, 1057) * mm, "end": v(-72.14, 1057) * mm});
            skLineSegment(sketch, "E191", {"start": v(-74.17, 1057) * mm, "end": v(-74.17, 1091.47) * mm});
            skSolve(sketch);
        }
        {
            var Q0;
            Q0 = qSketchRegion(id + "F56", true);
            var Q1;
            Q1=makeQuery(id+"F55.boolean.opBoolean","COPY",FACE,{"derivedFrom":makeQuery(id+"F55.opExtrude","SWEPT_FACE",FACE,{"disambiguationData":[OSD([sQuery(id+"F54.wireOp",EDGE,"E177.1")])]})});
            extrude(context, id + "F57", {"entities" : qUnion([Q0]), "endBound" : BoundingType.UP_TO_SURFACE, "endBoundEntityFace" : qUnion([Q1]), "depth" : 25.4 * mm});
        }
        {
            var Q0;
            Q0=makeQuery(id+"F57.opExtrude","SWEPT_FACE",FACE,{"disambiguationData":[OSD([sQuery(id+"F56.wireOp",EDGE,"E178.0"),sQuery(id+"F56.wireOp",EDGE,"E187.MirrorCS")])]});
            var sketch = newSketch(context, id + "F58", { "sketchPlane" : qUnion([Q0])});
            skLineSegment(sketch, "E192.bottom", {"start": v(-1953.77, 74.17) * mm, "end": v(-1950.6, 74.17) * mm});
            skLineSegment(sketch, "E192.top", {"start": v(-1953.77, -74.17) * mm, "end": v(-1950.6, -74.17) * mm});
            skLineSegment(sketch, "E192.left", {"start": v(-1953.77, 74.17) * mm, "end": v(-1953.77, -74.17) * mm});
            skLineSegment(sketch, "E192.right", {"start": v(-1950.6, 74.17) * mm, "end": v(-1950.6, -74.17) * mm});
            skLineSegment(sketch, "E193", {"start": v(0, 74.17) * mm, "end": v(0, 208.31) * mm, "construction": true});
            skLineSegment(sketch, "E194.MirrorCS", {"start": v(1953.77, -74.17) * mm, "end": v(1950.6, -74.17) * mm});
            skLineSegment(sketch, "E195.MirrorCS", {"start": v(1953.77, 74.17) * mm, "end": v(1950.6, 74.17) * mm});
            skLineSegment(sketch, "E196.MirrorCS", {"start": v(1953.77, 74.17) * mm, "end": v(1953.77, -74.17) * mm});
            skLineSegment(sketch, "E197.MirrorCS", {"start": v(1950.6, 74.17) * mm, "end": v(1950.6, -74.17) * mm});
            skCircle(sketch, "E198", {"center": v(0, 0) * mm, "radius": 53.98 * mm});
            skCircle(sketch, "E199", {"center": v(-1912.5, 61.47) * mm, "radius": 2.54 * mm});
            skLineSegment(sketch, "E200", {"start": v(-1912.5, 61.47) * mm, "end": v(0, 61.47) * mm, "construction": true});
            skCircle(sketch, "E201.1.0.0", {"center": v(-1593.74, 61.47) * mm, "radius": 2.54 * mm});
            skCircle(sketch, "E201.2.0.0", {"center": v(-1275, 61.47) * mm, "radius": 2.54 * mm});
            skCircle(sketch, "E201.3.0.0", {"center": v(-956.25, 61.47) * mm, "radius": 2.54 * mm});
            skCircle(sketch, "E201.4.0.0", {"center": v(-637.5, 61.47) * mm, "radius": 2.54 * mm});
            skLineSegment(sketch, "E201.direction1", {"start": v(-1912.5, 61.47) * mm, "end": v(-1593.74, 61.47) * mm, "construction": true});
            skLineSegment(sketch, "E201.direction2", {"start": v(-1912.5, 61.47) * mm, "end": v(-1912.5, -61.47) * mm, "construction": true});
            skLineSegment(sketch, "E202", {"start": v(0, 0) * mm, "end": v(-1953.77, 0) * mm, "construction": true});
            skLineSegment(sketch, "E203.MirrorCS", {"start": v(-1912.5, -61.47) * mm, "end": v(0, -61.47) * mm, "construction": true});
            skCircle(sketch, "E204.0.5.0", {"center": v(-318.75, 61.47) * mm, "radius": 2.54 * mm});
            skCircle(sketch, "E205.0.0.1", {"center": v(-1912.5, -61.47) * mm, "radius": 2.54 * mm});
            skCircle(sketch, "E205.0.1.1", {"center": v(-1593.74, -61.47) * mm, "radius": 2.54 * mm});
            skCircle(sketch, "E205.0.2.1", {"center": v(-1275, -61.47) * mm, "radius": 2.54 * mm});
            skCircle(sketch, "E205.0.3.1", {"center": v(-956.25, -61.47) * mm, "radius": 2.54 * mm});
            skCircle(sketch, "E205.0.4.1", {"center": v(-637.5, -61.47) * mm, "radius": 2.54 * mm});
            skCircle(sketch, "E205.0.5.1", {"center": v(-318.75, -61.47) * mm, "radius": 2.54 * mm});
            skCircle(sketch, "E206.0.6.0", {"center": v(0, 61.47) * mm, "radius": 2.54 * mm});
            skCircle(sketch, "E206.0.6.1", {"center": v(0, -61.47) * mm, "radius": 2.54 * mm});
            skCircle(sketch, "E206.0.7.0", {"center": v(318.75, 61.47) * mm, "radius": 2.54 * mm});
            skCircle(sketch, "E206.0.7.1", {"center": v(318.75, -61.47) * mm, "radius": 2.54 * mm});
            skCircle(sketch, "E206.0.8.0", {"center": v(637.5, 61.47) * mm, "radius": 2.54 * mm});
            skCircle(sketch, "E206.0.8.1", {"center": v(637.5, -61.47) * mm, "radius": 2.54 * mm});
            skCircle(sketch, "E206.0.9.0", {"center": v(956.25, 61.47) * mm, "radius": 2.54 * mm});
            skCircle(sketch, "E206.0.9.1", {"center": v(956.25, -61.47) * mm, "radius": 2.54 * mm});
            skCircle(sketch, "E206.0.10.0", {"center": v(1275, 61.47) * mm, "radius": 2.54 * mm});
            skCircle(sketch, "E206.0.10.1", {"center": v(1275, -61.47) * mm, "radius": 2.54 * mm});
            skCircle(sketch, "E207.0.11.0", {"center": v(1593.74, 61.47) * mm, "radius": 2.54 * mm});
            skCircle(sketch, "E207.0.11.1", {"center": v(1593.74, -61.47) * mm, "radius": 2.54 * mm});
            skCircle(sketch, "E207.0.12.0", {"center": v(1912.5, 61.47) * mm, "radius": 2.54 * mm});
            skCircle(sketch, "E207.0.12.1", {"center": v(1912.5, -61.47) * mm, "radius": 2.54 * mm});
            skSolve(sketch);
        }
        {
            var Q0;
            Q0 = qSketchRegion(id + "F58", true);
            extrude(context, id + "F59", {"entities" : qUnion([Q0]), "operationType" : NewBodyOperationType.REMOVE, "endBound" : BoundingType.THROUGH_ALL, "oppositeDirection" : true, "depth" : 25.4 * mm});
        }
        {
            var Q0;
            Q0=makeQuery(id+"F2.opExtrude","CAP_FACE",FACE,{"disambiguationData":[OSD([sQuery(id+"F1.wireOp",EDGE,"E56.0.0"),sQuery(id+"F1.wireOp",EDGE,"E56.0.1"),sQuery(id+"F1.wireOp",EDGE,"E56.0.2"),sQuery(id+"F1.wireOp",EDGE,"E56.0.3")])],"isStart":false});
            var sketch = newSketch(context, id + "F60", { "sketchPlane" : qUnion([Q0])});
            skLineSegment(sketch, "E208.0", {"start": v(1955.8, 1091.47) * mm, "end": v(-1955.8, 1091.47) * mm, "construction": true});
            skLineSegment(sketch, "E208.1", {"start": v(-1955.8, 1091.47) * mm, "end": v(-1955.8, 1053.37) * mm, "construction": true});
            skLineSegment(sketch, "E209", {"start": v(-1955.8, 1072.42) * mm, "end": v(1955.8, 1072.42) * mm, "construction": true});
            skLineSegment(sketch, "E210.0", {"start": v(1909.95, 1091.47) * mm, "end": v(1915.03, 1091.47) * mm, "construction": true});
            skPoint(sketch, "E211", {"position": v(1912.5, 1072.42) * mm});
            skPoint(sketch, "E211.positionSnap0", {"position": v(1912.5, 1091.47) * mm});
            skLineSegment(sketch, "E212.0", {"start": v(1272.46, 1091.47) * mm, "end": v(1277.54, 1091.47) * mm});
            skPoint(sketch, "E213", {"position": v(1275, 1072.42) * mm});
            skPoint(sketch, "E213.positionSnap0", {"position": v(1275, 1091.47) * mm});
            skLineSegment(sketch, "E214.0", {"start": v(634.96, 1091.47) * mm, "end": v(640.04, 1091.47) * mm, "construction": true});
            skPoint(sketch, "E215", {"position": v(637.5, 1072.42) * mm});
            skPoint(sketch, "E215.positionSnap0", {"position": v(637.5, 1091.47) * mm});
            skLineSegment(sketch, "E216.0", {"start": v(-2.54, 1091.47) * mm, "end": v(2.54, 1091.47) * mm, "construction": true});
            skPoint(sketch, "E217", {"position": v(0, 1072.42) * mm});
            skLineSegment(sketch, "E218.0", {"start": v(-640.04, 1091.47) * mm, "end": v(-634.96, 1091.47) * mm});
            skPoint(sketch, "E219", {"position": v(-637.5, 1072.42) * mm});
            skPoint(sketch, "E219.positionSnap0", {"position": v(-637.5, 1091.47) * mm});
            skLineSegment(sketch, "E220.0", {"start": v(-1277.54, 1091.47) * mm, "end": v(-1272.46, 1091.47) * mm});
            skPoint(sketch, "E221", {"position": v(-1275, 1072.42) * mm});
            skPoint(sketch, "E221.positionSnap0", {"position": v(-1275, 1091.47) * mm});
            skLineSegment(sketch, "E222.0", {"start": v(-1915.03, 1091.47) * mm, "end": v(-1909.95, 1091.47) * mm});
            skPoint(sketch, "E223", {"position": v(-1912.5, 1072.42) * mm});
            skPoint(sketch, "E223.positionSnap0", {"position": v(-1912.5, 1091.47) * mm});
            skSolve(sketch);
        }
        {
            var Q0;
            Q0=sQuery(id+"F60.wireOp",VERTEX,"E223");
            var Q1;
            Q1=sQuery(id+"F60.wireOp",VERTEX,"E221");
            var Q2;
            Q2=sQuery(id+"F60.wireOp",VERTEX,"E219");
            var Q3;
            Q3=sQuery(id+"F60.wireOp",VERTEX,"E217");
            var Q4;
            Q4=sQuery(id+"F60.wireOp",VERTEX,"E215");
            var Q5;
            Q5=sQuery(id+"F60.wireOp",VERTEX,"E213");
            var Q6;
            Q6=sQuery(id+"F60.wireOp",VERTEX,"E211");
            var Q7;
            Q7=makeQuery(id+"F2.opExtrude","SWEPT_BODY",BODY,{"disambiguationData":[OSD([sQuery(id+"F1.wireOp",EDGE,"E56.0.0"),sQuery(id+"F1.wireOp",EDGE,"E56.0.1"),sQuery(id+"F1.wireOp",EDGE,"E56.0.2"),sQuery(id+"F1.wireOp",EDGE,"E56.0.3")])]});
            var Q8;
            Q8=makeQuery(id+"F57.opExtrude","SWEPT_BODY",BODY,{"disambiguationData":[OSD([sQuery(id+"F56.wireOp",EDGE,"E178.0"),sQuery(id+"F56.wireOp",EDGE,"E179"),sQuery(id+"F56.wireOp",EDGE,"E180"),sQuery(id+"F56.wireOp",EDGE,"E181"),sQuery(id+"F56.wireOp",EDGE,"E182"),sQuery(id+"F56.wireOp",EDGE,"E186.MirrorCS"),sQuery(id+"F56.wireOp",EDGE,"E187.MirrorCS"),sQuery(id+"F56.wireOp",EDGE,"E189.MirrorCS"),sQuery(id+"F56.wireOp",EDGE,"E190.MirrorCS"),sQuery(id+"F56.wireOp",EDGE,"E191")])]});
            hole(context, id + "F61", {"style" : HoleStyle.C_SINK, "endStyle" : HoleEndStyle.BLIND_IN_LAST, "standardTappedOrClearance" : lookupTablePath({ "fit" : "Normal", "standard" : "ANSI", "engagement" : "75%", "pitch" : "32 tpi", "size" : "#8", "type" : "Clearance & tapped" }), "standardBlindInLast" : lookupTablePath({ "standard" : "ANSI", "fit" : "Free", "engagement" : "75%", "pitch" : "32 tpi", "size" : "#8", "type" : "Clearance & tapped" }), "holeDiameter" : 4.5 * mm, "cSinkDiameter" : 9.12 * mm, "cSinkAngle" : 82 * degree, "tapDrillDiameter" : 3.45 * mm, "showTappedDepth" : true, "holeDepth" : 15.08 * mm, "isTappedThrough" : true, "tappedDepth" : 12.7 * mm, "tapClearance" : 3, "locations" : qUnion([Q0, Q1, Q2, Q3, Q4, Q5, Q6]), "scope" : qUnion([Q7, Q8]), "majorDiameter" : 4.17 * mm, "startStyle" : HoleStartStyle.PART});
        }
        {
            var Q0;
            Q0=makeQuery(id+"F2.opExtrude","CAP_FACE",FACE,{"disambiguationData":[OSD([sQuery(id+"F1.wireOp",EDGE,"E56.0.0"),sQuery(id+"F1.wireOp",EDGE,"E56.0.1"),sQuery(id+"F1.wireOp",EDGE,"E56.0.2"),sQuery(id+"F1.wireOp",EDGE,"E56.0.3")])],"isStart":true});
            var sketch = newSketch(context, id + "F62", { "sketchPlane" : qUnion([Q0])});
            skLineSegment(sketch, "E224.0", {"start": v(-1955.8, 1091.47) * mm, "end": v(1955.8, 1091.47) * mm});
            skLineSegment(sketch, "E224.1", {"start": v(1955.8, 1091.47) * mm, "end": v(1955.8, 1053.37) * mm});
            skLineSegment(sketch, "E224.2", {"start": v(1955.8, 1072.42) * mm, "end": v(-1955.8, 1072.42) * mm, "construction": true});
            skLineSegment(sketch, "E224.3", {"start": v(-1909.95, 1091.47) * mm, "end": v(-1915.03, 1091.47) * mm});
            skPoint(sketch, "E224.4", {"position": v(-1912.5, 1072.42) * mm});
            skPoint(sketch, "E224.5", {"position": v(-1912.5, 1091.47) * mm});
            skLineSegment(sketch, "E224.6", {"start": v(-1272.46, 1091.47) * mm, "end": v(-1277.54, 1091.47) * mm});
            skPoint(sketch, "E224.7", {"position": v(-1275, 1072.42) * mm});
            skPoint(sketch, "E224.8", {"position": v(-1275, 1091.47) * mm});
            skLineSegment(sketch, "E224.9", {"start": v(-634.96, 1091.47) * mm, "end": v(-640.04, 1091.47) * mm});
            skPoint(sketch, "E224.10", {"position": v(-637.5, 1072.42) * mm});
            skPoint(sketch, "E224.11", {"position": v(-637.5, 1091.47) * mm});
            skLineSegment(sketch, "E224.12", {"start": v(2.54, 1091.47) * mm, "end": v(-2.54, 1091.47) * mm});
            skPoint(sketch, "E224.13", {"position": v(0, 1072.42) * mm});
            skLineSegment(sketch, "E224.14", {"start": v(640.04, 1091.47) * mm, "end": v(634.96, 1091.47) * mm});
            skPoint(sketch, "E224.15", {"position": v(637.5, 1072.42) * mm});
            skPoint(sketch, "E224.16", {"position": v(637.5, 1091.47) * mm});
            skLineSegment(sketch, "E224.17", {"start": v(1277.54, 1091.47) * mm, "end": v(1272.46, 1091.47) * mm});
            skPoint(sketch, "E224.18", {"position": v(1275, 1072.42) * mm});
            skPoint(sketch, "E224.19", {"position": v(1275, 1091.47) * mm});
            skLineSegment(sketch, "E224.20", {"start": v(1915.03, 1091.47) * mm, "end": v(1909.95, 1091.47) * mm});
            skPoint(sketch, "E224.21", {"position": v(1912.5, 1072.42) * mm});
            skPoint(sketch, "E224.22", {"position": v(1912.5, 1091.47) * mm});
            skSolve(sketch);
        }
        {
            var Q0;
            Q0=sQuery(id+"F62.wireOp",VERTEX,"E224.4");
            var Q1;
            Q1=sQuery(id+"F62.wireOp",VERTEX,"E224.7");
            var Q2;
            Q2=sQuery(id+"F62.wireOp",VERTEX,"E224.10");
            var Q3;
            Q3=sQuery(id+"F62.wireOp",VERTEX,"E224.13");
            var Q4;
            Q4=sQuery(id+"F62.wireOp",VERTEX,"E224.15");
            var Q5;
            Q5=sQuery(id+"F62.wireOp",VERTEX,"E224.18");
            var Q6;
            Q6=sQuery(id+"F62.wireOp",VERTEX,"E224.21");
            var Q7;
            Q7=makeQuery(id+"F2.opExtrude","SWEPT_BODY",BODY,{"disambiguationData":[OSD([sQuery(id+"F1.wireOp",EDGE,"E56.0.0"),sQuery(id+"F1.wireOp",EDGE,"E56.0.1"),sQuery(id+"F1.wireOp",EDGE,"E56.0.2"),sQuery(id+"F1.wireOp",EDGE,"E56.0.3")])]});
            var Q8;
            Q8=makeQuery(id+"F57.opExtrude","SWEPT_BODY",BODY,{"disambiguationData":[OSD([sQuery(id+"F56.wireOp",EDGE,"E178.0"),sQuery(id+"F56.wireOp",EDGE,"E179"),sQuery(id+"F56.wireOp",EDGE,"E180"),sQuery(id+"F56.wireOp",EDGE,"E181"),sQuery(id+"F56.wireOp",EDGE,"E182"),sQuery(id+"F56.wireOp",EDGE,"E186.MirrorCS"),sQuery(id+"F56.wireOp",EDGE,"E187.MirrorCS"),sQuery(id+"F56.wireOp",EDGE,"E189.MirrorCS"),sQuery(id+"F56.wireOp",EDGE,"E190.MirrorCS"),sQuery(id+"F56.wireOp",EDGE,"E191")])]});
            hole(context, id + "F63", {"style" : HoleStyle.C_SINK, "endStyle" : HoleEndStyle.BLIND_IN_LAST, "standardTappedOrClearance" : lookupTablePath({ "fit" : "Normal", "standard" : "ANSI", "engagement" : "75%", "pitch" : "32 tpi", "size" : "#8", "type" : "Clearance & tapped" }), "standardBlindInLast" : lookupTablePath({ "standard" : "ANSI", "fit" : "Free", "engagement" : "75%", "pitch" : "32 tpi", "size" : "#8", "type" : "Clearance & tapped" }), "holeDiameter" : 4.5 * mm, "cSinkDiameter" : 9.12 * mm, "cSinkAngle" : 82 * degree, "tapDrillDiameter" : 3.45 * mm, "showTappedDepth" : true, "holeDepth" : 15.1 * mm, "isTappedThrough" : true, "tappedDepth" : 12.7 * mm, "tapClearance" : 3, "locations" : qUnion([Q0, Q1, Q2, Q3, Q4, Q5, Q6]), "scope" : qUnion([Q7, Q8]), "majorDiameter" : 4.17 * mm, "startStyle" : HoleStartStyle.PART});
        }
        {
            var Q0;
            Q0=makeQuery(id+"F2.opExtrude","SWEPT_FACE",FACE,{"disambiguationData":[OSD([sQuery(id+"F1.wireOp",EDGE,"E56.0.1")])]});
            var sketch = newSketch(context, id + "F64", { "sketchPlane" : qUnion([Q0])});
            skCircle(sketch, "E225.0", {"center": v(1905, 0) * mm, "radius": 7.94 * mm, "construction": true});
            skCircle(sketch, "E225.1", {"center": v(1651, 0) * mm, "radius": 7.94 * mm, "construction": true});
            skCircle(sketch, "E225.2", {"center": v(1079.5, 0) * mm, "radius": 7.94 * mm, "construction": true});
            skCircle(sketch, "E225.3", {"center": v(825.5, 0) * mm, "radius": 7.94 * mm, "construction": true});
            skCircle(sketch, "E225.4", {"center": v(254, 0) * mm, "radius": 7.94 * mm, "construction": true});
            skCircle(sketch, "E225.5", {"center": v(0, 0) * mm, "radius": 7.94 * mm, "construction": true});
            skCircle(sketch, "E225.6", {"center": v(-254, 0) * mm, "radius": 7.94 * mm, "construction": true});
            skCircle(sketch, "E225.7", {"center": v(-825.5, 0) * mm, "radius": 7.94 * mm, "construction": true});
            skCircle(sketch, "E225.8", {"center": v(-1079.5, 0) * mm, "radius": 7.94 * mm, "construction": true});
            skCircle(sketch, "E225.9", {"center": v(-1651, 0) * mm, "radius": 7.94 * mm, "construction": true});
            skCircle(sketch, "E225.10", {"center": v(-1905, 0) * mm, "radius": 7.94 * mm, "construction": true});
            skCircle(sketch, "E226", {"center": v(-1905, 0) * mm, "radius": 9.53 * mm});
            skCircle(sketch, "E227", {"center": v(-1651, 0) * mm, "radius": 9.53 * mm});
            skCircle(sketch, "E228", {"center": v(-1079.5, 0) * mm, "radius": 9.53 * mm});
            skCircle(sketch, "E229", {"center": v(-825.5, 0) * mm, "radius": 9.53 * mm});
            skCircle(sketch, "E230", {"center": v(-254, 0) * mm, "radius": 9.52 * mm});
            skCircle(sketch, "E231", {"center": v(0, 0) * mm, "radius": 9.52 * mm});
            skCircle(sketch, "E232", {"center": v(254, 0) * mm, "radius": 9.53 * mm});
            skCircle(sketch, "E233", {"center": v(825.5, 0) * mm, "radius": 9.53 * mm});
            skCircle(sketch, "E234", {"center": v(1079.5, 0) * mm, "radius": 9.53 * mm});
            skCircle(sketch, "E235", {"center": v(1651, 0) * mm, "radius": 9.53 * mm});
            skCircle(sketch, "E236", {"center": v(1905, 0) * mm, "radius": 9.53 * mm});
            skSolve(sketch);
        }
        {
            var Q0;
            Q0 = qSketchRegion(id + "F64", true);
            extrude(context, id + "F65", {"entities" : qUnion([Q0]), "operationType" : NewBodyOperationType.REMOVE, "oppositeDirection" : true, "depth" : 25.4 * mm});
        }
    });
